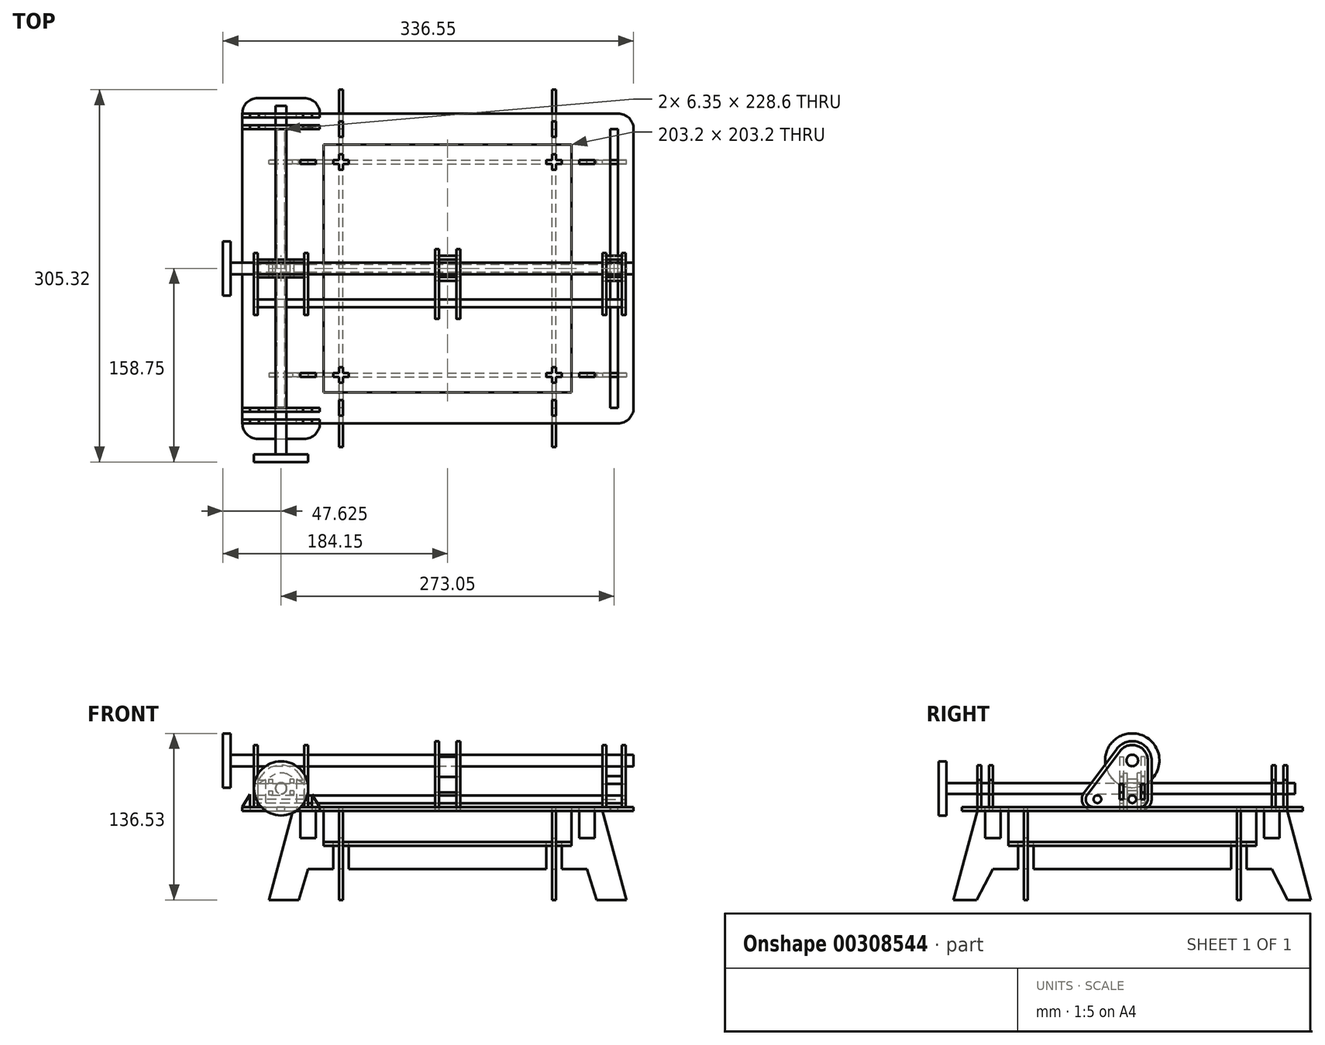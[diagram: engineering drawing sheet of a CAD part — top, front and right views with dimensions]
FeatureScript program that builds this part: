
annotation { "Feature Type Name" : "Feature", "Feature Type Description" : "" }
export const myFeature = defineFeature(function(context is Context, id is Id, definition is map)
    precondition{}
    {
        {
            var Q0;
            Q0=qCreatedBy(makeId("Top.planeOp"),FACE);
            var sketch = newSketch(context, id + "F0", { "sketchPlane" : qUnion([Q0])});
            skLineSegment(sketch, "E0.bottom", {"start": v(-101.6, 101.6) * mm, "end": v(101.6, 101.6) * mm});
            skLineSegment(sketch, "E0.top", {"start": v(-101.6, -101.6) * mm, "end": v(101.6, -101.6) * mm});
            skLineSegment(sketch, "E0.left", {"start": v(-101.6, 101.6) * mm, "end": v(-101.6, -101.6) * mm});
            skLineSegment(sketch, "E0.right", {"start": v(101.6, 101.6) * mm, "end": v(101.6, -101.6) * mm});
            skPoint(sketch, "E0.middle", {"position": v(0, 0) * mm});
            skSolve(sketch);
        }
        {
            var Q0;
            Q0=makeQuery(id+"F0.imprint","IMPRINT",FACE,{"disambiguationData":[TD([[makeQuery(id+"F0.imprint","IMPRINT",EDGE,{"derivedFrom":sQuery(id+"F0.wireOp",EDGE,"E0.bottom")}),-1.0]])]});
            extrude(context, id + "F1", {"entities" : qUnion([Q0]), "oppositeDirection" : true, "depth" : 3.17 * mm});
        }
        {
            var Q0;
            Q0=makeQuery(id+"F1.opExtrude","CAP_FACE",FACE,{"disambiguationData":[OSD([sQuery(id+"F0.wireOp",EDGE,"E0.bottom"),sQuery(id+"F0.wireOp",EDGE,"E0.top"),sQuery(id+"F0.wireOp",EDGE,"E0.left"),sQuery(id+"F0.wireOp",EDGE,"E0.right")])],"isStart":true});
            cPlane(context, id + "F2", {"entities" : qUnion([Q0]), "cplaneType" : CPlaneType.OFFSET, "offset" : 25.4 * mm, "width" : 152.4 * mm, "height" : 152.4 * mm});
        }
        {
            var Q0;
            Q0=qCreatedBy(id+"F2.planeOp",FACE);
            var sketch = newSketch(context, id + "F3", { "sketchPlane" : qUnion([Q0])});
            skLineSegment(sketch, "E1.bottom", {"start": v(-101.6, 101.6) * mm, "end": v(101.6, 101.6) * mm});
            skLineSegment(sketch, "E1.top", {"start": v(-101.6, -101.6) * mm, "end": v(101.6, -101.6) * mm});
            skLineSegment(sketch, "E1.left", {"start": v(-101.6, 101.6) * mm, "end": v(-101.6, -101.6) * mm});
            skLineSegment(sketch, "E1.right", {"start": v(101.6, 101.6) * mm, "end": v(101.6, -101.6) * mm});
            skPoint(sketch, "E1.middle", {"position": v(0, 0) * mm});
            skLineSegment(sketch, "E2.bottom", {"start": v(-114.3, 127) * mm, "end": v(114.3, 127) * mm});
            skLineSegment(sketch, "E2.top", {"start": v(-114.3, -127) * mm, "end": v(114.3, -127) * mm});
            skPoint(sketch, "E3.visualSharp", {"position": v(-127, 127) * mm});
            skPoint(sketch, "E4.visualSharp", {"position": v(127, 127) * mm});
            skPoint(sketch, "E5.visualSharp", {"position": v(127, -127) * mm});
            skPoint(sketch, "E6.visualSharp", {"position": v(-127, -127) * mm});
            skLineSegment(sketch, "E7.right", {"start": v(-152.4, 101.6) * mm, "end": v(-152.4, -101.6) * mm});
            skLineSegment(sketch, "E8.right", {"start": v(152.4, 101.6) * mm, "end": v(152.4, -101.6) * mm});
            skPoint(sketch, "E9.visualSharp", {"position": v(-152.4, 114.3) * mm});
            skPoint(sketch, "E10.visualSharp", {"position": v(-152.4, -114.3) * mm});
            skPoint(sketch, "E11.visualSharp", {"position": v(152.4, -114.3) * mm});
            skPoint(sketch, "E12.visualSharp", {"position": v(152.4, 114.3) * mm});
            skPoint(sketch, "E8.top.start.orphan", {"position": v(127, -114.3) * mm});
            skPoint(sketch, "E7.top.start.orphan", {"position": v(-127, -114.3) * mm});
            skLineSegment(sketch, "E13", {"start": v(-152.4, -101.6) * mm, "end": v(-152.4, -114.3) * mm});
            skLineSegment(sketch, "E14", {"start": v(-114.3, -127) * mm, "end": v(-139.7, -127) * mm});
            skLineSegment(sketch, "E15", {"start": v(114.3, -127) * mm, "end": v(139.7, -127) * mm});
            skLineSegment(sketch, "E16", {"start": v(152.4, -101.6) * mm, "end": v(152.4, -114.3) * mm});
            skLineSegment(sketch, "E17", {"start": v(152.4, 101.6) * mm, "end": v(152.4, 114.3) * mm});
            skLineSegment(sketch, "E18", {"start": v(114.3, 127) * mm, "end": v(139.7, 127) * mm});
            skLineSegment(sketch, "E19", {"start": v(-114.3, 127) * mm, "end": v(-139.7, 127) * mm});
            skLineSegment(sketch, "E20", {"start": v(-152.4, 101.6) * mm, "end": v(-152.4, 114.3) * mm});
            skPoint(sketch, "E21.visualSharp", {"position": v(-152.4, 127) * mm});
            skArc(sketch, "E21.filletArc", {"start": v(-139.7, 127) * mm, "mid": v(-148.68, 123.28) * mm, "end": v(-152.4, 114.3) * mm});
            skPoint(sketch, "E22.visualSharp", {"position": v(152.4, 127) * mm});
            skArc(sketch, "E22.filletArc", {"start": v(152.4, 114.3) * mm, "mid": v(148.68, 123.28) * mm, "end": v(139.7, 127) * mm});
            skPoint(sketch, "E23.visualSharp", {"position": v(152.4, -127) * mm});
            skArc(sketch, "E23.filletArc", {"start": v(139.7, -127) * mm, "mid": v(148.68, -123.28) * mm, "end": v(152.4, -114.3) * mm});
            skPoint(sketch, "E24.visualSharp", {"position": v(-152.4, -127) * mm});
            skArc(sketch, "E24.filletArc", {"start": v(-152.4, -114.3) * mm, "mid": v(-148.68, -123.28) * mm, "end": v(-139.7, -127) * mm});
            skSolve(sketch);
        }
        {
            var Q0;
            Q0=makeQuery(id+"F3.imprint","IMPRINT",FACE,{"disambiguationData":[TD([[makeQuery(id+"F3.imprint","IMPRINT",EDGE,{"derivedFrom":sQuery(id+"F3.wireOp",EDGE,"E1.bottom")}),1.0]])]});
            extrude(context, id + "F4", {"entities" : qUnion([Q0]), "depth" : 3.17 * mm});
        }
        {
            var Q0;
            Q0=makeQuery(id+"F4.opExtrude","CAP_FACE",FACE,{"disambiguationData":[OSD([sQuery(id+"F3.wireOp",EDGE,"E1.bottom"),sQuery(id+"F3.wireOp",EDGE,"E1.top"),sQuery(id+"F3.wireOp",EDGE,"E1.left"),sQuery(id+"F3.wireOp",EDGE,"E1.right"),sQuery(id+"F3.wireOp",EDGE,"E2.bottom"),sQuery(id+"F3.wireOp",EDGE,"E2.top"),sQuery(id+"F3.wireOp",EDGE,"E7.right"),sQuery(id+"F3.wireOp",EDGE,"E8.right"),sQuery(id+"F3.wireOp",EDGE,"E13"),sQuery(id+"F3.wireOp",EDGE,"E14"),sQuery(id+"F3.wireOp",EDGE,"E15"),sQuery(id+"F3.wireOp",EDGE,"E16"),sQuery(id+"F3.wireOp",EDGE,"E17"),sQuery(id+"F3.wireOp",EDGE,"E18"),sQuery(id+"F3.wireOp",EDGE,"E19"),sQuery(id+"F3.wireOp",EDGE,"E20"),sQuery(id+"F3.wireOp",EDGE,"E21.filletArc"),sQuery(id+"F3.wireOp",EDGE,"E22.filletArc"),sQuery(id+"F3.wireOp",EDGE,"E23.filletArc"),sQuery(id+"F3.wireOp",EDGE,"E24.filletArc")])],"isStart":false});
            var sketch = newSketch(context, id + "F5", { "sketchPlane" : qUnion([Q0])});
            skLineSegment(sketch, "E25.bottom", {"start": v(-155.58, -139.7) * mm, "end": v(-117.47, -139.7) * mm});
            skLineSegment(sketch, "E25.top", {"start": v(-155.57, 139.7) * mm, "end": v(-117.48, 139.7) * mm});
            skLineSegment(sketch, "E25.left", {"start": v(-168.28, -127) * mm, "end": v(-168.27, 127) * mm});
            skLineSegment(sketch, "E25.right", {"start": v(-104.77, -127) * mm, "end": v(-104.77, 127) * mm});
            skPoint(sketch, "E25.middle", {"position": v(-136.53, 0) * mm});
            skPoint(sketch, "E26.visualSharp", {"position": v(-104.77, 139.7) * mm});
            skArc(sketch, "E26.filletArc", {"start": v(-104.78, 127) * mm, "mid": v(-108.5, 135.98) * mm, "end": v(-117.48, 139.7) * mm});
            skPoint(sketch, "E27.visualSharp", {"position": v(-168.27, 139.7) * mm});
            skArc(sketch, "E27.filletArc", {"start": v(-155.57, 139.7) * mm, "mid": v(-164.56, 135.98) * mm, "end": v(-168.27, 127) * mm});
            skPoint(sketch, "E28.visualSharp", {"position": v(-168.28, -139.7) * mm});
            skArc(sketch, "E28.filletArc", {"start": v(-168.28, -127) * mm, "mid": v(-164.56, -135.98) * mm, "end": v(-155.58, -139.7) * mm});
            skPoint(sketch, "E29.visualSharp", {"position": v(-104.77, -139.7) * mm});
            skArc(sketch, "E29.filletArc", {"start": v(-117.47, -139.7) * mm, "mid": v(-108.5, -135.98) * mm, "end": v(-104.77, -127) * mm});
            skSolve(sketch);
        }
        {
            var Q0;
            Q0 = qSketchRegion(id + "F5", true);
            extrude(context, id + "F6", {"entities" : qUnion([Q0]), "operationType" : NewBodyOperationType.ADD, "oppositeDirection" : true, "depth" : 3.17 * mm});
        }
        {
            var Q0;
            Q0=makeQuery(id+"F4.opExtrude","CAP_FACE",FACE,{"disambiguationData":[OSD([sQuery(id+"F3.wireOp",EDGE,"E1.bottom"),sQuery(id+"F3.wireOp",EDGE,"E1.top"),sQuery(id+"F3.wireOp",EDGE,"E1.left"),sQuery(id+"F3.wireOp",EDGE,"E1.right"),sQuery(id+"F3.wireOp",EDGE,"E2.bottom"),sQuery(id+"F3.wireOp",EDGE,"E2.top"),sQuery(id+"F3.wireOp",EDGE,"E2.left"),sQuery(id+"F3.wireOp",EDGE,"E2.right"),sQuery(id+"F3.wireOp",EDGE,"E3.filletArc"),sQuery(id+"F3.wireOp",EDGE,"E4.filletArc"),sQuery(id+"F3.wireOp",EDGE,"E5.filletArc"),sQuery(id+"F3.wireOp",EDGE,"E6.filletArc")])],"isStart":false});
            var sketch = newSketch(context, id + "F7", { "sketchPlane" : qUnion([Q0])});
            skLineSegment(sketch, "E30.bottom", {"start": v(-133.35, -114.3) * mm, "end": v(-139.7, -114.3) * mm});
            skLineSegment(sketch, "E30.top", {"start": v(-133.35, 114.3) * mm, "end": v(-139.7, 114.3) * mm});
            skLineSegment(sketch, "E30.left", {"start": v(-133.35, -114.3) * mm, "end": v(-133.35, 114.3) * mm});
            skLineSegment(sketch, "E30.right", {"start": v(-139.7, -114.3) * mm, "end": v(-139.7, 114.3) * mm});
            skPoint(sketch, "E30.middle", {"position": v(-136.53, 0) * mm});
            skLineSegment(sketch, "E31", {"start": v(0, 87.2) * mm, "end": v(0, -86.86) * mm, "construction": true});
            skLineSegment(sketch, "E32.MirrorCS", {"start": v(133.35, -114.3) * mm, "end": v(139.7, -114.3) * mm});
            skLineSegment(sketch, "E33.MirrorCS", {"start": v(133.35, 114.3) * mm, "end": v(139.7, 114.3) * mm});
            skPoint(sketch, "E34.MirrorP", {"position": v(136.53, 0) * mm});
            skLineSegment(sketch, "E35.MirrorCS", {"start": v(133.35, -114.3) * mm, "end": v(133.35, 114.3) * mm});
            skLineSegment(sketch, "E36.MirrorCS", {"start": v(139.7, -114.3) * mm, "end": v(139.7, 114.3) * mm});
            skSolve(sketch);
        }
        {
            var Q0;
            Q0=qCreatedBy(makeId("Right.planeOp"),FACE);
            cPlane(context, id + "F8", {"entities" : qUnion([Q0]), "cplaneType" : CPlaneType.OFFSET, "offset" : 88.9 * mm, "oppositeDirection" : true, "width" : 152.4 * mm, "height" : 152.4 * mm});
        }
        {
            var Q0;
            Q0=qCreatedBy(id+"F8.planeOp",FACE);
            var sketch = newSketch(context, id + "F9", { "sketchPlane" : qUnion([Q0])});
            skLineSegment(sketch, "E37", {"start": v(0, -3.18) * mm, "end": v(80.96, -3.18) * mm});
            skLineSegment(sketch, "E38", {"start": v(101.6, -3.18) * mm, "end": v(101.6, 0) * mm});
            skLineSegment(sketch, "E39", {"start": v(101.6, 0) * mm, "end": v(101.6, 25.4) * mm});
            skLineSegment(sketch, "E40", {"start": v(101.6, 25.4) * mm, "end": v(107.95, 25.4) * mm});
            skLineSegment(sketch, "E41", {"start": v(127, 25.4) * mm, "end": v(146.57, -47.63) * mm});
            skLineSegment(sketch, "E42", {"start": v(146.57, -47.62) * mm, "end": v(127.52, -47.62) * mm});
            skLineSegment(sketch, "E43", {"start": v(127.52, -47.62) * mm, "end": v(114.3, -22.23) * mm});
            skLineSegment(sketch, "E44", {"start": v(114.3, -22.22) * mm, "end": v(88.9, -22.22) * mm});
            skLineSegment(sketch, "E45", {"start": v(0, 51.23) * mm, "end": v(0, 12.05) * mm, "construction": true});
            skLineSegment(sketch, "E46", {"start": v(120.65, 25.4) * mm, "end": v(120.65, 28.58) * mm});
            skLineSegment(sketch, "E47", {"start": v(120.65, 28.58) * mm, "end": v(107.95, 28.58) * mm});
            skLineSegment(sketch, "E48", {"start": v(107.95, 28.58) * mm, "end": v(107.95, 25.4) * mm});
            skLineSegment(sketch, "E49.trimOffspring", {"start": v(120.65, 25.4) * mm, "end": v(127, 25.4) * mm});
            skLineSegment(sketch, "E50", {"start": v(93.66, -3.17) * mm, "end": v(93.66, 0) * mm});
            skLineSegment(sketch, "E51", {"start": v(93.66, 0) * mm, "end": v(80.96, 0) * mm});
            skLineSegment(sketch, "E52", {"start": v(80.96, 0) * mm, "end": v(80.96, -3.17) * mm});
            skLineSegment(sketch, "E53.trimOffspring", {"start": v(93.66, -3.18) * mm, "end": v(101.6, -3.18) * mm});
            skLineSegment(sketch, "E54.MirrorCS", {"start": v(-101.6, -3.18) * mm, "end": v(-101.6, 0) * mm});
            skLineSegment(sketch, "E55.MirrorCS", {"start": v(-101.6, 25.4) * mm, "end": v(-107.95, 25.4) * mm});
            skLineSegment(sketch, "E56.MirrorCS", {"start": v(-80.96, 0) * mm, "end": v(-80.96, -3.18) * mm});
            skLineSegment(sketch, "E57.MirrorCS", {"start": v(-93.66, -3.18) * mm, "end": v(-93.66, 0) * mm});
            skLineSegment(sketch, "E58.MirrorCS", {"start": v(-107.95, 28.58) * mm, "end": v(-107.95, 25.4) * mm});
            skLineSegment(sketch, "E59.MirrorCS", {"start": v(-120.65, 25.4) * mm, "end": v(-127, 25.4) * mm});
            skLineSegment(sketch, "E60.MirrorCS", {"start": v(-120.65, 25.4) * mm, "end": v(-120.65, 28.58) * mm});
            skLineSegment(sketch, "E61.MirrorCS", {"start": v(-93.66, 0) * mm, "end": v(-80.96, 0) * mm});
            skLineSegment(sketch, "E62.MirrorCS", {"start": v(-93.66, -3.18) * mm, "end": v(-101.6, -3.18) * mm});
            skLineSegment(sketch, "E63.MirrorCS", {"start": v(-101.6, 0) * mm, "end": v(-101.6, 25.4) * mm});
            skLineSegment(sketch, "E64.MirrorCS", {"start": v(-127, 25.4) * mm, "end": v(-146.57, -47.63) * mm});
            skLineSegment(sketch, "E65.MirrorCS", {"start": v(-146.57, -47.62) * mm, "end": v(-127.52, -47.62) * mm});
            skLineSegment(sketch, "E66.MirrorCS", {"start": v(-127.52, -47.63) * mm, "end": v(-114.3, -22.23) * mm});
            skLineSegment(sketch, "E67.MirrorCS", {"start": v(-120.65, 28.58) * mm, "end": v(-107.95, 28.58) * mm});
            skLineSegment(sketch, "E68.MirrorCS", {"start": v(0, -3.18) * mm, "end": v(-80.96, -3.18) * mm});
            skLineSegment(sketch, "E69.MirrorCS", {"start": v(-114.3, -22.22) * mm, "end": v(-88.9, -22.22) * mm});
            skLineSegment(sketch, "E70.top", {"start": v(88.9, -10.8) * mm, "end": v(85.73, -10.8) * mm});
            skLineSegment(sketch, "E70.left", {"start": v(88.9, -22.22) * mm, "end": v(88.9, -10.8) * mm});
            skLineSegment(sketch, "E70.right", {"start": v(85.73, -22.22) * mm, "end": v(85.73, -10.8) * mm});
            skLineSegment(sketch, "E71.MirrorCS", {"start": v(-85.73, -22.22) * mm, "end": v(-85.73, -10.8) * mm});
            skLineSegment(sketch, "E72.MirrorCS", {"start": v(-88.9, -22.22) * mm, "end": v(-88.9, -10.8) * mm});
            skLineSegment(sketch, "E73.MirrorCS", {"start": v(-88.9, -10.8) * mm, "end": v(-85.73, -10.8) * mm});
            skLineSegment(sketch, "E74.trimOffspring", {"start": v(-85.73, -22.22) * mm, "end": v(0, -22.23) * mm});
            skLineSegment(sketch, "E75.trimOffspring", {"start": v(85.73, -22.22) * mm, "end": v(0, -22.23) * mm});
            skSolve(sketch);
        }
        {
            var Q0;
            Q0=makeQuery(id+"F9.imprint","IMPRINT",FACE,{"disambiguationData":[TD([[makeQuery(id+"F9.imprint","IMPRINT",EDGE,{"derivedFrom":sQuery(id+"F9.wireOp",EDGE,"E37")}),-1.0]])]});
            extrude(context, id + "F10", {"entities" : qUnion([Q0]), "depth" : 3.17 * mm});
        }
        {
            var Q0;
            Q0=makeQuery(id+"F10.opExtrude","SWEPT_BODY",BODY,{"disambiguationData":[OSD([sQuery(id+"F9.wireOp",EDGE,"E37"),sQuery(id+"F9.wireOp",EDGE,"E38"),sQuery(id+"F9.wireOp",EDGE,"E39"),sQuery(id+"F9.wireOp",EDGE,"E40"),sQuery(id+"F9.wireOp",EDGE,"E41"),sQuery(id+"F9.wireOp",EDGE,"E42"),sQuery(id+"F9.wireOp",EDGE,"E43"),sQuery(id+"F9.wireOp",EDGE,"E44"),sQuery(id+"F9.wireOp",EDGE,"E46"),sQuery(id+"F9.wireOp",EDGE,"E47"),sQuery(id+"F9.wireOp",EDGE,"E48"),sQuery(id+"F9.wireOp",EDGE,"E49.trimOffspring"),sQuery(id+"F9.wireOp",EDGE,"E50"),sQuery(id+"F9.wireOp",EDGE,"E51"),sQuery(id+"F9.wireOp",EDGE,"E52"),sQuery(id+"F9.wireOp",EDGE,"E53.trimOffspring"),sQuery(id+"F9.wireOp",EDGE,"E54.MirrorCS"),sQuery(id+"F9.wireOp",EDGE,"E55.MirrorCS"),sQuery(id+"F9.wireOp",EDGE,"E56.MirrorCS"),sQuery(id+"F9.wireOp",EDGE,"E57.MirrorCS"),sQuery(id+"F9.wireOp",EDGE,"E58.MirrorCS"),sQuery(id+"F9.wireOp",EDGE,"E59.MirrorCS"),sQuery(id+"F9.wireOp",EDGE,"E60.MirrorCS"),sQuery(id+"F9.wireOp",EDGE,"E61.MirrorCS"),sQuery(id+"F9.wireOp",EDGE,"E62.MirrorCS"),sQuery(id+"F9.wireOp",EDGE,"E63.MirrorCS"),sQuery(id+"F9.wireOp",EDGE,"E64.MirrorCS"),sQuery(id+"F9.wireOp",EDGE,"E65.MirrorCS"),sQuery(id+"F9.wireOp",EDGE,"E66.MirrorCS"),sQuery(id+"F9.wireOp",EDGE,"E67.MirrorCS"),sQuery(id+"F9.wireOp",EDGE,"E68.MirrorCS"),sQuery(id+"F9.wireOp",EDGE,"E69.MirrorCS")])]});
            var Q1;
            Q1=qCreatedBy(makeId("Right.planeOp"),FACE);
            mirror(context, id + "F11", {"entities" : qUnion([Q0]), "mirrorPlane" : qUnion([Q1])});
        }
        {
            var Q0;
            Q0=qCreatedBy(makeId("Front.planeOp"),FACE);
            cPlane(context, id + "F12", {"entities" : qUnion([Q0]), "cplaneType" : CPlaneType.OFFSET, "offset" : 88.9 * mm, "width" : 152.4 * mm, "height" : 152.4 * mm});
        }
        {
            var Q0;
            Q0=qCreatedBy(id+"F12.planeOp",FACE);
            var sketch = newSketch(context, id + "F13", { "sketchPlane" : qUnion([Q0])});
            skLineSegment(sketch, "E76", {"start": v(-101.6, -3.18) * mm, "end": v(-101.6, 0) * mm});
            skLineSegment(sketch, "E77", {"start": v(-101.6, 0) * mm, "end": v(-101.6, 25.4) * mm});
            skLineSegment(sketch, "E78", {"start": v(-101.6, 25.4) * mm, "end": v(-107.95, 25.4) * mm});
            skLineSegment(sketch, "E79", {"start": v(-107.95, 25.4) * mm, "end": v(-107.95, 28.58) * mm});
            skLineSegment(sketch, "E80", {"start": v(-107.95, 28.58) * mm, "end": v(-120.65, 28.58) * mm});
            skLineSegment(sketch, "E81", {"start": v(-120.65, 28.58) * mm, "end": v(-120.65, 25.4) * mm});
            skLineSegment(sketch, "E82", {"start": v(-120.65, 25.4) * mm, "end": v(-127, 25.4) * mm});
            skLineSegment(sketch, "E83", {"start": v(-127, 25.4) * mm, "end": v(-146.57, -47.63) * mm});
            skLineSegment(sketch, "E84", {"start": v(-146.57, -47.63) * mm, "end": v(-122.04, -47.63) * mm});
            skLineSegment(sketch, "E85", {"start": v(-122.04, -47.63) * mm, "end": v(-114.3, -22.22) * mm});
            skLineSegment(sketch, "E86", {"start": v(-114.3, -22.22) * mm, "end": v(0, -22.22) * mm});
            skLineSegment(sketch, "E87.0", {"start": v(0, -3.18) * mm, "end": v(-80.96, -3.18) * mm});
            skPoint(sketch, "E88.start.orphan", {"position": v(0, -11.05) * mm});
            skLineSegment(sketch, "E89", {"start": v(-93.66, -3.18) * mm, "end": v(-93.66, 0) * mm});
            skLineSegment(sketch, "E90", {"start": v(-93.66, 0) * mm, "end": v(-88.9, 0) * mm});
            skLineSegment(sketch, "E91", {"start": v(-80.96, 0) * mm, "end": v(-80.96, -3.18) * mm});
            skLineSegment(sketch, "E92", {"start": v(0, 50.7) * mm, "end": v(0, 10.1) * mm, "construction": true});
            skLineSegment(sketch, "E93.MirrorCS", {"start": v(101.6, -3.18) * mm, "end": v(101.6, 0) * mm});
            skLineSegment(sketch, "E94.MirrorCS", {"start": v(107.95, 25.4) * mm, "end": v(107.95, 28.58) * mm});
            skLineSegment(sketch, "E95.MirrorCS", {"start": v(120.65, 28.58) * mm, "end": v(120.65, 25.4) * mm});
            skLineSegment(sketch, "E96.MirrorCS", {"start": v(120.65, 25.4) * mm, "end": v(127, 25.4) * mm});
            skLineSegment(sketch, "E97.MirrorCS", {"start": v(101.6, 25.4) * mm, "end": v(107.95, 25.4) * mm});
            skLineSegment(sketch, "E98.MirrorCS", {"start": v(107.95, 28.58) * mm, "end": v(120.65, 28.58) * mm});
            skLineSegment(sketch, "E99.MirrorCS", {"start": v(122.04, -47.63) * mm, "end": v(114.3, -22.22) * mm});
            skLineSegment(sketch, "E100.MirrorCS", {"start": v(80.96, 0) * mm, "end": v(80.96, -3.17) * mm});
            skLineSegment(sketch, "E101.MirrorCS", {"start": v(93.66, 0) * mm, "end": v(88.9, 0) * mm});
            skLineSegment(sketch, "E102.MirrorCS", {"start": v(93.66, -3.17) * mm, "end": v(93.66, 0) * mm});
            skLineSegment(sketch, "E103.MirrorCS", {"start": v(101.6, 0) * mm, "end": v(101.6, 25.4) * mm});
            skLineSegment(sketch, "E104.MirrorCS", {"start": v(146.57, -47.63) * mm, "end": v(122.04, -47.63) * mm});
            skLineSegment(sketch, "E105.MirrorCS", {"start": v(127, 25.4) * mm, "end": v(146.57, -47.63) * mm});
            skLineSegment(sketch, "E106.MirrorCS", {"start": v(114.3, -22.22) * mm, "end": v(0, -22.22) * mm});
            skLineSegment(sketch, "E107.MirrorCS", {"start": v(0, -3.18) * mm, "end": v(80.96, -3.18) * mm});
            skLineSegment(sketch, "E108.trimOffspring", {"start": v(-93.66, -3.18) * mm, "end": v(-101.6, -3.18) * mm});
            skLineSegment(sketch, "E109.trimOffspring", {"start": v(93.66, -3.18) * mm, "end": v(101.6, -3.18) * mm});
            skLineSegment(sketch, "E110.top", {"start": v(-88.9, -11.43) * mm, "end": v(-85.73, -11.43) * mm});
            skLineSegment(sketch, "E110.left", {"start": v(-88.9, 0) * mm, "end": v(-88.9, -11.43) * mm});
            skLineSegment(sketch, "E110.right", {"start": v(-85.73, 0) * mm, "end": v(-85.73, -11.43) * mm});
            skLineSegment(sketch, "E111.MirrorCS", {"start": v(85.73, 0) * mm, "end": v(85.73, -11.43) * mm});
            skLineSegment(sketch, "E112.MirrorCS", {"start": v(88.9, 0) * mm, "end": v(88.9, -11.43) * mm});
            skLineSegment(sketch, "E113.MirrorCS", {"start": v(88.9, -11.43) * mm, "end": v(85.73, -11.43) * mm});
            skLineSegment(sketch, "E114.trimOffspring", {"start": v(-85.73, 0) * mm, "end": v(-80.96, 0) * mm});
            skLineSegment(sketch, "E115.trimOffspring", {"start": v(85.73, 0) * mm, "end": v(80.96, 0) * mm});
            skSolve(sketch);
        }
        {
            var Q0;
            {var subQ2=sQuery(id+"F13.wireOp",EDGE,"E76");Q0=makeQuery(id+"F13.imprint","IMPRINT",FACE,{"disambiguationData":[TD([[makeQuery(id+"F13.imprint","IMPRINT",EDGE,{"derivedFrom":subQ2}),1.0]])]});}
            extrude(context, id + "F14", {"entities" : qUnion([Q0]), "oppositeDirection" : true, "depth" : 3.17 * mm});
        }
        {
            var Q0;
            Q0=makeQuery(id+"F14.opExtrude","SWEPT_BODY",BODY,{"disambiguationData":[OSD([sQuery(id+"F13.wireOp",EDGE,"E76"),sQuery(id+"F13.wireOp",EDGE,"E77"),sQuery(id+"F13.wireOp",EDGE,"E78"),sQuery(id+"F13.wireOp",EDGE,"E79"),sQuery(id+"F13.wireOp",EDGE,"E80"),sQuery(id+"F13.wireOp",EDGE,"E81"),sQuery(id+"F13.wireOp",EDGE,"E82"),sQuery(id+"F13.wireOp",EDGE,"E83"),sQuery(id+"F13.wireOp",EDGE,"E84"),sQuery(id+"F13.wireOp",EDGE,"E85"),sQuery(id+"F13.wireOp",EDGE,"E86"),sQuery(id+"F13.wireOp",EDGE,"E87.0"),sQuery(id+"F13.wireOp",EDGE,"E89"),sQuery(id+"F13.wireOp",EDGE,"E90"),sQuery(id+"F13.wireOp",EDGE,"E91"),sQuery(id+"F13.wireOp",EDGE,"E98.MirrorCS"),sQuery(id+"F13.wireOp",EDGE,"E95.MirrorCS"),sQuery(id+"F13.wireOp",EDGE,"E96.MirrorCS"),sQuery(id+"F13.wireOp",EDGE,"E93.MirrorCS"),sQuery(id+"F13.wireOp",EDGE,"E94.MirrorCS"),sQuery(id+"F13.wireOp",EDGE,"E97.MirrorCS"),sQuery(id+"F13.wireOp",EDGE,"E102.MirrorCS"),sQuery(id+"F13.wireOp",EDGE,"E101.MirrorCS"),sQuery(id+"F13.wireOp",EDGE,"E100.MirrorCS"),sQuery(id+"F13.wireOp",EDGE,"E104.MirrorCS"),sQuery(id+"F13.wireOp",EDGE,"E105.MirrorCS"),sQuery(id+"F13.wireOp",EDGE,"E103.MirrorCS"),sQuery(id+"F13.wireOp",EDGE,"E99.MirrorCS"),sQuery(id+"F13.wireOp",EDGE,"E106.MirrorCS"),sQuery(id+"F13.wireOp",EDGE,"E107.MirrorCS"),sQuery(id+"F13.wireOp",EDGE,"E108.trimOffspring"),sQuery(id+"F13.wireOp",EDGE,"E109.trimOffspring")])]});
            var Q1;
            Q1=qCreatedBy(makeId("Front.planeOp"),FACE);
            mirror(context, id + "F15", {"entities" : qUnion([Q0]), "mirrorPlane" : qUnion([Q1])});
        }
        {
            var Q0;
            Q0=makeQuery(id+"F7.imprint","IMPRINT",FACE,{"disambiguationData":[TD([[makeQuery(id+"F7.imprint","IMPRINT",EDGE,{"derivedFrom":sQuery(id+"F7.wireOp",EDGE,"E30.bottom")}),-1.0]])]});
            var Q1;
            Q1=makeQuery(id+"F7.imprint","IMPRINT",FACE,{"disambiguationData":[TD([[makeQuery(id+"F7.imprint","IMPRINT",EDGE,{"derivedFrom":sQuery(id+"F7.wireOp",EDGE,"E32.MirrorCS")}),1.0]])]});
            extrude(context, id + "F16", {"entities" : qUnion([Q0, Q1]), "operationType" : NewBodyOperationType.REMOVE, "oppositeDirection" : true, "depth" : 8.13 * mm});
        }
        {
            var Q0;
            Q0=qCreatedBy(makeId("Front.planeOp"),FACE);
            cPlane(context, id + "F17", {"entities" : qUnion([Q0]), "cplaneType" : CPlaneType.OFFSET, "offset" : 114.3 * mm, "width" : 152.4 * mm, "height" : 152.4 * mm});
        }
        {
            var Q0;
            Q0=qCreatedBy(id+"F17.planeOp",FACE);
            var sketch = newSketch(context, id + "F18", { "sketchPlane" : qUnion([Q0])});
            skCircle(sketch, "E116", {"center": v(-136.53, 43.82) * mm, "radius": 4.76 * mm});
            skArc(sketch, "E117", {"start": v(-120.3, 53.8) * mm, "mid": v(-136.53, 62.87) * mm, "end": v(-152.75, 53.8) * mm});
            skLineSegment(sketch, "E118", {"start": v(-168.28, 28.58) * mm, "end": v(-161.93, 28.58) * mm});
            skLineSegment(sketch, "E119", {"start": v(-161.93, 28.58) * mm, "end": v(-161.93, 25.4) * mm});
            skLineSegment(sketch, "E120", {"start": v(-161.93, 25.4) * mm, "end": v(-149.23, 25.4) * mm});
            skLineSegment(sketch, "E121", {"start": v(-149.23, 25.4) * mm, "end": v(-149.23, 28.58) * mm});
            skLineSegment(sketch, "E122", {"start": v(-123.83, 28.58) * mm, "end": v(-123.83, 25.4) * mm});
            skLineSegment(sketch, "E123", {"start": v(-123.83, 25.4) * mm, "end": v(-111.13, 25.4) * mm});
            skLineSegment(sketch, "E124", {"start": v(-111.12, 25.4) * mm, "end": v(-111.12, 28.58) * mm});
            skLineSegment(sketch, "E125.trimOffspring", {"start": v(-111.12, 28.58) * mm, "end": v(-104.78, 28.58) * mm});
            skLineSegment(sketch, "E126.trimOffspring", {"start": v(-149.23, 28.58) * mm, "end": v(-123.83, 28.58) * mm});
            skLineSegment(sketch, "E127", {"start": v(-168.28, 28.58) * mm, "end": v(-152.75, 53.8) * mm});
            skLineSegment(sketch, "E128", {"start": v(-104.78, 28.58) * mm, "end": v(-120.3, 53.8) * mm});
            skSolve(sketch);
        }
        {
            var Q0;
            Q0=makeQuery(id+"F18.imprint","IMPRINT",FACE,{"disambiguationData":[TD([[makeQuery(id+"F18.imprint","IMPRINT",EDGE,{"derivedFrom":sQuery(id+"F18.wireOp",EDGE,"E116")}),-1.0]])]});
            extrude(context, id + "F19", {"entities" : qUnion([Q0]), "depth" : 3.17 * mm});
        }
        {
            var Q0;
            Q0=qCreatedBy(id+"F17.planeOp",FACE);
            cPlane(context, id + "F20", {"entities" : qUnion([Q0]), "cplaneType" : CPlaneType.OFFSET, "offset" : 6.35 * mm, "width" : 152.4 * mm, "height" : 152.4 * mm});
        }
        {
            var Q0;
            Q0=makeQuery(id+"F19.opExtrude","SWEPT_BODY",BODY,{"disambiguationData":[OSD([sQuery(id+"F18.wireOp",EDGE,"E116"),sQuery(id+"F18.wireOp",EDGE,"E117"),sQuery(id+"F18.wireOp",EDGE,"38bzoTGT-MK2d-pk2N-3JFI-UJTJc2NmZi06"),sQuery(id+"F18.wireOp",EDGE,"pucSDfX4-3BOz-H23i-j3uv-TdQ4Dl5jIXsU"),sQuery(id+"F18.wireOp",EDGE,"E118")])]});
            var Q1;
            Q1=qCreatedBy(id+"F20.planeOp",FACE);
            mirror(context, id + "F21", {"entities" : qUnion([Q0]), "mirrorPlane" : qUnion([Q1])});
        }
        {
            var Q0;
            Q0=makeQuery(id+"F21.opPattern","COPY",BODY,{"derivedFrom":makeQuery(id+"F19.opExtrude","SWEPT_BODY",BODY,{"disambiguationData":[OSD([sQuery(id+"F18.wireOp",EDGE,"E116"),sQuery(id+"F18.wireOp",EDGE,"E117"),sQuery(id+"F18.wireOp",EDGE,"38bzoTGT-MK2d-pk2N-3JFI-UJTJc2NmZi06"),sQuery(id+"F18.wireOp",EDGE,"pucSDfX4-3BOz-H23i-j3uv-TdQ4Dl5jIXsU"),sQuery(id+"F18.wireOp",EDGE,"E118")])]}),"instanceName":"1"});
            var Q1;
            Q1=makeQuery(id+"F19.opExtrude","SWEPT_BODY",BODY,{"disambiguationData":[OSD([sQuery(id+"F18.wireOp",EDGE,"E116"),sQuery(id+"F18.wireOp",EDGE,"E117"),sQuery(id+"F18.wireOp",EDGE,"38bzoTGT-MK2d-pk2N-3JFI-UJTJc2NmZi06"),sQuery(id+"F18.wireOp",EDGE,"pucSDfX4-3BOz-H23i-j3uv-TdQ4Dl5jIXsU"),sQuery(id+"F18.wireOp",EDGE,"E118")])]});
            var Q2;
            Q2=qCreatedBy(makeId("Front.planeOp"),FACE);
            mirror(context, id + "F22", {"entities" : qUnion([Q0, Q1]), "mirrorPlane" : qUnion([Q2])});
        }
        {
            var Q0;
            Q0=qCreatedBy(makeId("Right.planeOp"),FACE);
            cPlane(context, id + "F23", {"entities" : qUnion([Q0]), "cplaneType" : CPlaneType.OFFSET, "offset" : 114.3 * mm, "oppositeDirection" : true, "width" : 152.4 * mm, "height" : 152.4 * mm});
        }
        {
            var Q0;
            Q0=qCreatedBy(makeId("Right.planeOp"),FACE);
            cPlane(context, id + "F24", {"entities" : qUnion([Q0]), "cplaneType" : CPlaneType.OFFSET, "offset" : 136.53 * mm, "oppositeDirection" : true, "width" : 152.4 * mm, "height" : 152.4 * mm});
        }
        {
            var Q0;
            Q0=qCreatedBy(id+"F23.planeOp",FACE);
            var sketch = newSketch(context, id + "F25", { "sketchPlane" : qUnion([Q0])});
            skCircle(sketch, "E129", {"center": v(0, 66.68) * mm, "radius": 4.76 * mm});
            skArc(sketch, "E130", {"start": v(12.7, 66.68) * mm, "mid": v(4.02, 78.72) * mm, "end": v(-10.16, 74.3) * mm});
            skLineSegment(sketch, "E131", {"start": v(12.7, 66.68) * mm, "end": v(12.7, 34.93) * mm});
            skLineSegment(sketch, "E132", {"start": v(-10.16, 74.3) * mm, "end": v(-36.83, 38.73) * mm});
            skLineSegment(sketch, "E133", {"start": v(6.35, 28.58) * mm, "end": v(-31.75, 28.58) * mm});
            skCircle(sketch, "E134", {"center": v(0, 34.93) * mm, "radius": 3.18 * mm});
            skCircle(sketch, "E135", {"center": v(-28.57, 34.92) * mm, "radius": 3.18 * mm});
            skPoint(sketch, "E136.visualSharp", {"position": v(12.7, 28.58) * mm});
            skPoint(sketch, "E137.visualSharp", {"position": v(-44.45, 28.57) * mm});
            skArc(sketch, "E138.filletArc", {"start": v(6.35, 28.58) * mm, "mid": v(10.84, 30.43) * mm, "end": v(12.7, 34.93) * mm});
            skArc(sketch, "E139.filletArc", {"start": v(-36.83, 38.73) * mm, "mid": v(-37.43, 32.09) * mm, "end": v(-31.75, 28.57) * mm});
            skSolve(sketch);
        }
        {
            var Q0;
            Q0=makeQuery(id+"F25.imprint","IMPRINT",FACE,{"disambiguationData":[TD([[makeQuery(id+"F25.imprint","IMPRINT",EDGE,{"derivedFrom":sQuery(id+"F25.wireOp",EDGE,"E129")}),-1.0]])]});
            extrude(context, id + "F26", {"entities" : qUnion([Q0]), "oppositeDirection" : true, "depth" : 3.17 * mm});
        }
        {
            var Q0;
            Q0=makeQuery(id+"F26.opExtrude","SWEPT_BODY",BODY,{"disambiguationData":[OSD([sQuery(id+"F25.wireOp",EDGE,"E129"),sQuery(id+"F25.wireOp",EDGE,"E130"),sQuery(id+"F25.wireOp",EDGE,"E131"),sQuery(id+"F25.wireOp",EDGE,"E132"),sQuery(id+"F25.wireOp",EDGE,"E133")])]});
            var Q1;
            Q1=qCreatedBy(id+"F24.planeOp",FACE);
            mirror(context, id + "F27", {"entities" : qUnion([Q0]), "mirrorPlane" : qUnion([Q1])});
        }
        {
            var Q0;
            Q0=qCreatedBy(makeId("Front.planeOp"),FACE);
            cPlane(context, id + "F28", {"entities" : qUnion([Q0]), "cplaneType" : CPlaneType.OFFSET, "offset" : 7.14 * mm, "width" : 152.4 * mm, "height" : 152.4 * mm});
        }
        {
            var Q0;
            Q0=qCreatedBy(makeId("Front.planeOp"),FACE);
            cPlane(context, id + "F29", {"entities" : qUnion([Q0]), "cplaneType" : CPlaneType.OFFSET, "offset" : 4.17 * mm, "width" : 152.4 * mm, "height" : 152.4 * mm});
        }
        {
            var Q0;
            Q0=qCreatedBy(id+"F29.planeOp",FACE);
            var sketch = newSketch(context, id + "F30", { "sketchPlane" : qUnion([Q0])});
            skLineSegment(sketch, "E140.bottom", {"start": v(-155.58, 28.58) * mm, "end": v(-139.7, 28.58) * mm});
            skLineSegment(sketch, "E140.top", {"start": v(-155.58, 60.33) * mm, "end": v(-117.48, 60.33) * mm});
            skLineSegment(sketch, "E140.left", {"start": v(-155.58, 28.58) * mm, "end": v(-155.58, 34.93) * mm});
            skLineSegment(sketch, "E140.right", {"start": v(-117.48, 28.58) * mm, "end": v(-117.48, 34.93) * mm});
            skCircle(sketch, "E141", {"center": v(-136.53, 43.82) * mm, "radius": 4.76 * mm});
            skLineSegment(sketch, "E142", {"start": v(-155.58, 47.63) * mm, "end": v(-158.75, 47.63) * mm});
            skLineSegment(sketch, "E143", {"start": v(-158.75, 47.63) * mm, "end": v(-158.75, 34.93) * mm});
            skLineSegment(sketch, "E144", {"start": v(-158.75, 34.93) * mm, "end": v(-155.58, 34.93) * mm});
            skLineSegment(sketch, "E145", {"start": v(-117.48, 47.63) * mm, "end": v(-114.3, 47.63) * mm});
            skLineSegment(sketch, "E146", {"start": v(-114.3, 47.63) * mm, "end": v(-114.3, 34.93) * mm});
            skLineSegment(sketch, "E147", {"start": v(-114.3, 34.93) * mm, "end": v(-117.48, 34.93) * mm});
            skLineSegment(sketch, "E148.trimOffspring", {"start": v(-117.48, 47.63) * mm, "end": v(-117.48, 60.33) * mm});
            skLineSegment(sketch, "E149.trimOffspring", {"start": v(-155.58, 47.63) * mm, "end": v(-155.58, 60.33) * mm});
            skLineSegment(sketch, "E150", {"start": v(-139.7, 28.58) * mm, "end": v(-139.7, 25.4) * mm});
            skLineSegment(sketch, "E151", {"start": v(-139.7, 25.4) * mm, "end": v(-133.35, 25.4) * mm});
            skLineSegment(sketch, "E152", {"start": v(-133.35, 25.4) * mm, "end": v(-133.35, 28.58) * mm});
            skLineSegment(sketch, "E153.trimOffspring", {"start": v(-133.35, 28.58) * mm, "end": v(-117.48, 28.58) * mm});
            skArc(sketch, "E154", {"start": v(-130.27, 54.87) * mm, "mid": v(-136.53, 56.52) * mm, "end": v(-142.78, 54.87) * mm});
            skLineSegment(sketch, "E155", {"start": v(-155.58, 47.63) * mm, "end": v(-142.78, 54.87) * mm});
            skLineSegment(sketch, "E156", {"start": v(-117.48, 47.63) * mm, "end": v(-130.27, 54.87) * mm});
            skSolve(sketch);
        }
        {
            var Q0;
            Q0=makeQuery(id+"F30.imprint","IMPRINT",FACE,{"disambiguationData":[TD([[makeQuery(id+"F30.imprint","IMPRINT",EDGE,{"derivedFrom":sQuery(id+"F30.wireOp",EDGE,"E140.bottom")}),1.0]])]});
            extrude(context, id + "F31", {"entities" : qUnion([Q0]), "depth" : 3.17 * mm});
        }
        {
            var Q0;
            Q0=makeQuery(id+"F31.opExtrude","SWEPT_BODY",BODY,{"disambiguationData":[OSD([sQuery(id+"F30.wireOp",EDGE,"E140.bottom"),sQuery(id+"F30.wireOp",EDGE,"E140.top"),sQuery(id+"F30.wireOp",EDGE,"E140.left"),sQuery(id+"F30.wireOp",EDGE,"E140.right"),sQuery(id+"F30.wireOp",EDGE,"E141"),sQuery(id+"F30.wireOp",EDGE,"E142"),sQuery(id+"F30.wireOp",EDGE,"E143"),sQuery(id+"F30.wireOp",EDGE,"E144"),sQuery(id+"F30.wireOp",EDGE,"E145"),sQuery(id+"F30.wireOp",EDGE,"E146"),sQuery(id+"F30.wireOp",EDGE,"E147"),sQuery(id+"F30.wireOp",EDGE,"E148.trimOffspring"),sQuery(id+"F30.wireOp",EDGE,"E149.trimOffspring"),sQuery(id+"F30.wireOp",EDGE,"E150"),sQuery(id+"F30.wireOp",EDGE,"E151"),sQuery(id+"F30.wireOp",EDGE,"E152"),sQuery(id+"F30.wireOp",EDGE,"E153.trimOffspring")])]});
            var Q1;
            Q1=qCreatedBy(makeId("Front.planeOp"),FACE);
            mirror(context, id + "F32", {"entities" : qUnion([Q0]), "mirrorPlane" : qUnion([Q1])});
        }
        {
            var Q0;
            Q0=qCreatedBy(makeId("Right.planeOp"),FACE);
            cPlane(context, id + "F33", {"entities" : qUnion([Q0]), "cplaneType" : CPlaneType.OFFSET, "offset" : 127 * mm, "width" : 152.4 * mm, "height" : 152.4 * mm});
        }
        {
            var Q0;
            Q0=qCreatedBy(id+"F33.planeOp",FACE);
            var sketch = newSketch(context, id + "F34", { "sketchPlane" : qUnion([Q0])});
            skArc(sketch, "E157.0", {"start": v(12.7, 66.68) * mm, "mid": v(4.02, 78.72) * mm, "end": v(-10.16, 74.3) * mm});
            skLineSegment(sketch, "E158.0", {"start": v(12.7, 66.68) * mm, "end": v(12.7, 66.68) * mm});
            skLineSegment(sketch, "E159.0", {"start": v(-10.16, 74.3) * mm, "end": v(-10.16, 74.3) * mm});
            skCircle(sketch, "E160.0", {"center": v(0, 66.68) * mm, "radius": 4.76 * mm});
            skCircle(sketch, "E161.0", {"center": v(-28.57, 34.92) * mm, "radius": 3.18 * mm});
            skCircle(sketch, "E162.0", {"center": v(0, 34.93) * mm, "radius": 3.18 * mm});
            skLineSegment(sketch, "E163.0", {"start": v(-10.16, 74.3) * mm, "end": v(-36.83, 38.73) * mm});
            skArc(sketch, "E164.0", {"start": v(-36.83, 38.73) * mm, "mid": v(-37.43, 32.09) * mm, "end": v(-31.75, 28.57) * mm});
            skArc(sketch, "E165.0", {"start": v(6.35, 28.58) * mm, "mid": v(10.84, 30.43) * mm, "end": v(12.7, 34.93) * mm});
            skLineSegment(sketch, "E166.0", {"start": v(6.35, 28.58) * mm, "end": v(-31.75, 28.58) * mm});
            skLineSegment(sketch, "E167.0", {"start": v(12.7, 66.68) * mm, "end": v(12.7, 34.93) * mm});
            skSolve(sketch);
        }
        {
            var Q0;
            Q0=makeQuery(id+"F34.imprint","IMPRINT",FACE,{"disambiguationData":[TD([[makeQuery(id+"F34.imprint","IMPRINT",EDGE,{"derivedFrom":sQuery(id+"F34.wireOp",EDGE,"E160.0")}),-1.0]])]});
            extrude(context, id + "F35", {"entities" : qUnion([Q0]), "depth" : 3.17 * mm});
        }
        {
            var Q0;
            Q0=qCreatedBy(makeId("Right.planeOp"),FACE);
            cPlane(context, id + "F36", {"entities" : qUnion([Q0]), "cplaneType" : CPlaneType.OFFSET, "offset" : 136.53 * mm, "width" : 152.4 * mm, "height" : 152.4 * mm});
        }
        {
            var Q0;
            Q0=makeQuery(id+"F35.opExtrude","SWEPT_BODY",BODY,{"disambiguationData":[OSD([sQuery(id+"F34.wireOp",EDGE,"E157.0"),sQuery(id+"F34.wireOp",EDGE,"E158.0"),sQuery(id+"F34.wireOp",EDGE,"628ac780-78d9-4351-907e-1ec801662de6.0"),sQuery(id+"F34.wireOp",EDGE,"E159.0"),sQuery(id+"F34.wireOp",EDGE,"E160.0")])]});
            var Q1;
            Q1=qCreatedBy(id+"F36.planeOp",FACE);
            mirror(context, id + "F37", {"entities" : qUnion([Q0]), "mirrorPlane" : qUnion([Q1])});
        }
        {
            var Q0;
            Q0=qCreatedBy(makeId("Right.planeOp"),FACE);
            var sketch = newSketch(context, id + "F38", { "sketchPlane" : qUnion([Q0])});
            skCircle(sketch, "E168.0", {"center": v(-28.57, 34.92) * mm, "radius": 3.18 * mm});
            skCircle(sketch, "E169.0", {"center": v(0, 34.93) * mm, "radius": 3.18 * mm});
            skSolve(sketch);
        }
        {
            var Q0;
            Q0 = qSketchRegion(id + "F38", true);
            extrude(context, id + "F39", {"entities" : qUnion([Q0]), "depth" : 146.05 * mm, "hasSecondDirection" : true, "secondDirectionOppositeDirection" : true, "secondDirectionDepth" : 158.75 * mm});
        }
        {
            var Q0;
            Q0=qCreatedBy(makeId("Right.planeOp"),FACE);
            cPlane(context, id + "F40", {"entities" : qUnion([Q0]), "cplaneType" : CPlaneType.OFFSET, "offset" : 7.14 * mm, "width" : 152.4 * mm, "height" : 152.4 * mm});
        }
        {
            var Q0;
            Q0=qCreatedBy(id+"F40.planeOp",FACE);
            var sketch = newSketch(context, id + "F41", { "sketchPlane" : qUnion([Q0])});
            skCircle(sketch, "E170", {"center": v(0, 66.68) * mm, "radius": 4.76 * mm});
            skArc(sketch, "E171", {"start": v(15.88, 66.68) * mm, "mid": v(5.02, 81.74) * mm, "end": v(-12.7, 76.2) * mm});
            skLineSegment(sketch, "E172", {"start": v(-12.7, 76.2) * mm, "end": v(-39.37, 40.64) * mm});
            skLineSegment(sketch, "E173", {"start": v(15.88, 66.68) * mm, "end": v(15.88, 34.93) * mm});
            skLineSegment(sketch, "E174", {"start": v(-31.75, 25.4) * mm, "end": v(6.35, 25.4) * mm});
            skPoint(sketch, "E175.visualSharp", {"position": v(-50.8, 25.4) * mm});
            skArc(sketch, "E175.filletArc", {"start": v(-39.37, 40.64) * mm, "mid": v(-40.27, 30.67) * mm, "end": v(-31.75, 25.4) * mm});
            skPoint(sketch, "E176.visualSharp", {"position": v(15.88, 25.4) * mm});
            skArc(sketch, "E176.filletArc", {"start": v(6.35, 25.4) * mm, "mid": v(13.09, 28.19) * mm, "end": v(15.88, 34.93) * mm});
            skCircle(sketch, "E177", {"center": v(0, 34.93) * mm, "radius": 3.3 * mm});
            skCircle(sketch, "E178", {"center": v(-28.57, 34.92) * mm, "radius": 3.3 * mm});
            skSolve(sketch);
        }
        {
            var Q0;
            Q0=makeQuery(id+"F41.imprint","IMPRINT",FACE,{"disambiguationData":[TD([[makeQuery(id+"F41.imprint","IMPRINT",EDGE,{"derivedFrom":sQuery(id+"F41.wireOp",EDGE,"E170")}),-1.0]])]});
            extrude(context, id + "F42", {"entities" : qUnion([Q0]), "depth" : 3.17 * mm});
        }
        {
            var Q0;
            Q0=makeQuery(id+"F42.opExtrude","SWEPT_BODY",BODY,{"disambiguationData":[OSD([sQuery(id+"F41.wireOp",EDGE,"E170"),sQuery(id+"F41.wireOp",EDGE,"E171"),sQuery(id+"F41.wireOp",EDGE,"E172"),sQuery(id+"F41.wireOp",EDGE,"E173"),sQuery(id+"F41.wireOp",EDGE,"E174"),sQuery(id+"F41.wireOp",EDGE,"E175.filletArc"),sQuery(id+"F41.wireOp",EDGE,"E176.filletArc"),sQuery(id+"F41.wireOp",EDGE,"E177"),sQuery(id+"F41.wireOp",EDGE,"E178")])]});
            var Q1;
            Q1=qCreatedBy(makeId("Right.planeOp"),FACE);
            mirror(context, id + "F43", {"entities" : qUnion([Q0]), "mirrorPlane" : qUnion([Q1])});
        }
        {
            var Q0;
            Q0=qCreatedBy(makeId("Right.planeOp"),FACE);
            var sketch = newSketch(context, id + "F44", { "sketchPlane" : qUnion([Q0])});
            skCircle(sketch, "E179", {"center": v(0, 66.68) * mm, "radius": 4.76 * mm});
            skSolve(sketch);
        }
        {
            var Q0;
            Q0=makeQuery(id+"F44.imprint","IMPRINT",FACE,{"disambiguationData":[TD([[makeQuery(id+"F44.imprint","IMPRINT",EDGE,{"derivedFrom":sQuery(id+"F44.wireOp",EDGE,"E179")}),1.0]])]});
            extrude(context, id + "F45", {"entities" : qUnion([Q0]), "depth" : 152.4 * mm, "hasSecondDirection" : true, "secondDirectionOppositeDirection" : true, "secondDirectionDepth" : 177.8 * mm});
        }
        {
            var Q0;
            Q0=qCreatedBy(makeId("Front.planeOp"),FACE);
            var sketch = newSketch(context, id + "F46", { "sketchPlane" : qUnion([Q0])});
            skCircle(sketch, "E180", {"center": v(-136.53, 43.82) * mm, "radius": 4.45 * mm});
            skSolve(sketch);
        }
        {
            var Q0;
            Q0=makeQuery(id+"F46.imprint","IMPRINT",FACE,{"disambiguationData":[TD([[makeQuery(id+"F46.imprint","IMPRINT",EDGE,{"derivedFrom":sQuery(id+"F46.wireOp",EDGE,"E180")}),1.0]])]});
            extrude(context, id + "F47", {"entities" : qUnion([Q0]), "depth" : 152.4 * mm, "hasSecondDirection" : true, "secondDirectionOppositeDirection" : true, "secondDirectionDepth" : 133.35 * mm});
        }
        {
            var Q0;
            Q0=qCreatedBy(id+"F28.planeOp",FACE);
            var sketch = newSketch(context, id + "F48", { "sketchPlane" : qUnion([Q0])});
            skLineSegment(sketch, "E181.bottom", {"start": v(130.18, 53.98) * mm, "end": v(142.88, 53.98) * mm});
            skLineSegment(sketch, "E181.top", {"start": v(130.18, 28.58) * mm, "end": v(133.48, 28.58) * mm});
            skLineSegment(sketch, "E181.left", {"start": v(130.18, 53.98) * mm, "end": v(130.18, 47.62) * mm});
            skLineSegment(sketch, "E181.right", {"start": v(142.88, 53.98) * mm, "end": v(142.88, 47.63) * mm});
            skLineSegment(sketch, "E182", {"start": v(133.48, 28.58) * mm, "end": v(133.48, 25.4) * mm});
            skLineSegment(sketch, "E183", {"start": v(133.48, 25.4) * mm, "end": v(139.57, 25.4) * mm});
            skLineSegment(sketch, "E184", {"start": v(139.57, 25.4) * mm, "end": v(139.57, 28.58) * mm});
            skLineSegment(sketch, "E185", {"start": v(130.18, 47.62) * mm, "end": v(127, 47.62) * mm});
            skLineSegment(sketch, "E186", {"start": v(127, 47.63) * mm, "end": v(127, 34.93) * mm});
            skLineSegment(sketch, "E187", {"start": v(127, 34.92) * mm, "end": v(130.18, 34.92) * mm});
            skLineSegment(sketch, "E188", {"start": v(142.88, 47.63) * mm, "end": v(146.05, 47.63) * mm});
            skLineSegment(sketch, "E189", {"start": v(146.05, 47.63) * mm, "end": v(146.05, 34.93) * mm});
            skLineSegment(sketch, "E190", {"start": v(146.05, 34.93) * mm, "end": v(142.88, 34.93) * mm});
            skLineSegment(sketch, "E191.trimOffspring", {"start": v(142.88, 34.93) * mm, "end": v(142.88, 28.58) * mm});
            skLineSegment(sketch, "E192.trimOffspring", {"start": v(130.18, 34.92) * mm, "end": v(130.18, 28.58) * mm});
            skLineSegment(sketch, "E193.trimOffspring", {"start": v(139.57, 28.58) * mm, "end": v(142.88, 28.58) * mm});
            skSolve(sketch);
        }
        {
            var Q0;
            Q0=makeQuery(id+"F48.imprint","IMPRINT",FACE,{"disambiguationData":[TD([[makeQuery(id+"F48.imprint","IMPRINT",EDGE,{"derivedFrom":sQuery(id+"F48.wireOp",EDGE,"E181.bottom")}),-1.0]])]});
            extrude(context, id + "F49", {"entities" : qUnion([Q0]), "depth" : 3.17 * mm});
        }
        {
            var Q0;
            Q0=makeQuery(id+"F49.opExtrude","SWEPT_BODY",BODY,{"disambiguationData":[OSD([sQuery(id+"F48.wireOp",EDGE,"E181.bottom"),sQuery(id+"F48.wireOp",EDGE,"E181.top"),sQuery(id+"F48.wireOp",EDGE,"E181.left"),sQuery(id+"F48.wireOp",EDGE,"E181.right"),sQuery(id+"F48.wireOp",EDGE,"E182"),sQuery(id+"F48.wireOp",EDGE,"E183"),sQuery(id+"F48.wireOp",EDGE,"E184"),sQuery(id+"F48.wireOp",EDGE,"E185"),sQuery(id+"F48.wireOp",EDGE,"E186"),sQuery(id+"F48.wireOp",EDGE,"E187"),sQuery(id+"F48.wireOp",EDGE,"E188"),sQuery(id+"F48.wireOp",EDGE,"E189"),sQuery(id+"F48.wireOp",EDGE,"E190"),sQuery(id+"F48.wireOp",EDGE,"E191.trimOffspring"),sQuery(id+"F48.wireOp",EDGE,"E192.trimOffspring"),sQuery(id+"F48.wireOp",EDGE,"E193.trimOffspring")])]});
            var Q1;
            Q1=qCreatedBy(makeId("Front.planeOp"),FACE);
            mirror(context, id + "F50", {"entities" : qUnion([Q0]), "mirrorPlane" : qUnion([Q1])});
        }
        {
            var Q0;
            Q0=makeQuery(id+"F47.opExtrude","CAP_FACE",FACE,{"disambiguationData":[OSD([sQuery(id+"F46.wireOp",EDGE,"E180")])],"isStart":false});
            var sketch = newSketch(context, id + "F51", { "sketchPlane" : qUnion([Q0])});
            skCircle(sketch, "E194", {"center": v(-136.53, 43.82) * mm, "radius": 22.23 * mm});
            skSolve(sketch);
        }
        {
            var Q0;
            Q0=makeQuery(id+"F51.imprint","IMPRINT",FACE,{"disambiguationData":[TD([[makeQuery(id+"F51.imprint","IMPRINT",EDGE,{"derivedFrom":sQuery(id+"F51.wireOp",EDGE,"E194")}),1.0]])]});
            var Q1;
            Q1=makeQuery(id+"F51.imprint","IMPRINT",FACE,{"disambiguationData":[TD([[makeQuery(id+"F51.imprint","IMPRINT",EDGE,{"derivedFrom":makeQuery(id+"F47.opExtrude","CAP_EDGE",EDGE,{"disambiguationData":[OSD([sQuery(id+"F46.wireOp",EDGE,"E180")])],"isStart":false})}),1.0]])]});
            extrude(context, id + "F52", {"entities" : qUnion([Q0, Q1]), "operationType" : NewBodyOperationType.ADD, "depth" : 6.35 * mm});
        }
        {
            var Q0;
            Q0=makeQuery(id+"F45.opExtrude","CAP_FACE",FACE,{"disambiguationData":[OSD([sQuery(id+"F44.wireOp",EDGE,"E179")])],"isStart":true});
            var sketch = newSketch(context, id + "F53", { "sketchPlane" : qUnion([Q0])});
            skCircle(sketch, "E195", {"center": v(0, 66.68) * mm, "radius": 22.23 * mm});
            skSolve(sketch);
        }
        {
            var Q0;
            Q0=makeQuery(id+"F53.imprint","IMPRINT",FACE,{"disambiguationData":[TD([[makeQuery(id+"F53.imprint","IMPRINT",EDGE,{"derivedFrom":makeQuery(id+"F45.opExtrude","CAP_EDGE",EDGE,{"disambiguationData":[OSD([sQuery(id+"F44.wireOp",EDGE,"E179")])],"isStart":true})}),-1.0]])]});
            var Q1;
            Q1=makeQuery(id+"F53.imprint","IMPRINT",FACE,{"disambiguationData":[TD([[makeQuery(id+"F53.imprint","IMPRINT",EDGE,{"derivedFrom":sQuery(id+"F53.wireOp",EDGE,"E195")}),1.0]])]});
            extrude(context, id + "F54", {"entities" : qUnion([Q0, Q1]), "operationType" : NewBodyOperationType.ADD, "depth" : 6.35 * mm});
        }
        {
            var Q0;
            Q0=qCreatedBy(id+"F28.planeOp",FACE);
            var sketch = newSketch(context, id + "F55", { "sketchPlane" : qUnion([Q0])});
            skLineSegment(sketch, "E196.bottom", {"start": v(-7.14, 69.85) * mm, "end": v(7.14, 69.85) * mm});
            skLineSegment(sketch, "E196.top", {"start": v(-7.14, 31.75) * mm, "end": v(7.14, 31.75) * mm});
            skLineSegment(sketch, "E196.left", {"start": v(-7.14, 69.85) * mm, "end": v(-7.14, 31.75) * mm});
            skLineSegment(sketch, "E196.right", {"start": v(7.14, 69.85) * mm, "end": v(7.14, 31.75) * mm});
            skLineSegment(sketch, "E197", {"start": v(-7.14, 53.34) * mm, "end": v(-10.32, 53.34) * mm});
            skLineSegment(sketch, "E198", {"start": v(-10.32, 53.34) * mm, "end": v(-10.32, 40.64) * mm});
            skLineSegment(sketch, "E199", {"start": v(-10.32, 40.64) * mm, "end": v(-7.14, 40.64) * mm});
            skLineSegment(sketch, "E200", {"start": v(7.14, 53.34) * mm, "end": v(10.32, 53.34) * mm});
            skLineSegment(sketch, "E201", {"start": v(10.32, 53.34) * mm, "end": v(10.32, 40.64) * mm});
            skLineSegment(sketch, "E202", {"start": v(10.32, 40.64) * mm, "end": v(7.14, 40.64) * mm});
            skSolve(sketch);
        }
        {
            var Q0;
            Q0 = qSketchRegion(id + "F55", true);
            extrude(context, id + "F56", {"entities" : qUnion([Q0]), "depth" : 3.17 * mm});
        }
        {
            var Q0;
            Q0=makeQuery(id+"F56.opExtrude","SWEPT_BODY",BODY,{"disambiguationData":[OSD([sQuery(id+"F55.wireOp",EDGE,"E196.bottom"),sQuery(id+"F55.wireOp",EDGE,"E196.top"),sQuery(id+"F55.wireOp",EDGE,"E196.left"),sQuery(id+"F55.wireOp",EDGE,"E196.right"),sQuery(id+"F55.wireOp",EDGE,"E197"),sQuery(id+"F55.wireOp",EDGE,"E198"),sQuery(id+"F55.wireOp",EDGE,"E199"),sQuery(id+"F55.wireOp",EDGE,"E200"),sQuery(id+"F55.wireOp",EDGE,"E201"),sQuery(id+"F55.wireOp",EDGE,"E202")])]});
            var Q1;
            Q1=qCreatedBy(makeId("Front.planeOp"),FACE);
            mirror(context, id + "F57", {"entities" : qUnion([Q0]), "mirrorPlane" : qUnion([Q1])});
        }
        {
            var Q0;
            Q0=qCreatedBy(makeId("Right.planeOp"),FACE);
            cPlane(context, id + "F58", {"entities" : qUnion([Q0]), "cplaneType" : CPlaneType.OFFSET, "offset" : 136.53 * mm, "oppositeDirection" : true, "width" : 152.4 * mm, "height" : 152.4 * mm});
        }
        {
            var Q0;
            Q0=qCreatedBy(makeId("Right.planeOp"),FACE);
            cPlane(context, id + "F59", {"entities" : qUnion([Q0]), "cplaneType" : CPlaneType.OFFSET, "offset" : 129.38 * mm, "oppositeDirection" : true, "width" : 152.4 * mm, "height" : 152.4 * mm});
        }
        {
            var Q0;
            Q0=qCreatedBy(id+"F59.planeOp",FACE);
            var sketch = newSketch(context, id + "F60", { "sketchPlane" : qUnion([Q0])});
            skLineSegment(sketch, "E203.bottom", {"start": v(4.17, 51.44) * mm, "end": v(-4.17, 51.44) * mm});
            skLineSegment(sketch, "E203.top", {"start": v(4.17, 38.74) * mm, "end": v(-4.17, 38.74) * mm});
            skLineSegment(sketch, "E203.left", {"start": v(4.17, 51.44) * mm, "end": v(4.17, 48.26) * mm});
            skLineSegment(sketch, "E203.right", {"start": v(-4.17, 51.44) * mm, "end": v(-4.17, 48.26) * mm});
            skLineSegment(sketch, "E204", {"start": v(-4.17, 48.26) * mm, "end": v(-7.34, 48.26) * mm});
            skLineSegment(sketch, "E205", {"start": v(-7.34, 48.26) * mm, "end": v(-7.34, 41.91) * mm});
            skLineSegment(sketch, "E206", {"start": v(-7.34, 41.91) * mm, "end": v(-4.17, 41.91) * mm});
            skLineSegment(sketch, "E207", {"start": v(4.17, 48.26) * mm, "end": v(7.34, 48.26) * mm});
            skLineSegment(sketch, "E208", {"start": v(7.34, 48.26) * mm, "end": v(7.34, 41.91) * mm});
            skLineSegment(sketch, "E209", {"start": v(7.34, 41.91) * mm, "end": v(4.17, 41.91) * mm});
            skLineSegment(sketch, "E210.trimOffspring", {"start": v(4.17, 41.91) * mm, "end": v(4.17, 38.74) * mm});
            skLineSegment(sketch, "E211.trimOffspring", {"start": v(-4.17, 41.91) * mm, "end": v(-4.17, 38.74) * mm});
            skSolve(sketch);
        }
        {
            var Q0;
            Q0 = qSketchRegion(id + "F60", true);
            extrude(context, id + "F61", {"entities" : qUnion([Q0]), "depth" : 3.17 * mm});
        }
        {
            var Q0;
            Q0=makeQuery(id+"F61.opExtrude","SWEPT_BODY",BODY,{"disambiguationData":[OSD([sQuery(id+"F60.wireOp",EDGE,"E203.bottom"),sQuery(id+"F60.wireOp",EDGE,"E203.top"),sQuery(id+"F60.wireOp",EDGE,"E203.left"),sQuery(id+"F60.wireOp",EDGE,"E203.right"),sQuery(id+"F60.wireOp",EDGE,"E204"),sQuery(id+"F60.wireOp",EDGE,"E205"),sQuery(id+"F60.wireOp",EDGE,"E206"),sQuery(id+"F60.wireOp",EDGE,"E207"),sQuery(id+"F60.wireOp",EDGE,"E208"),sQuery(id+"F60.wireOp",EDGE,"E209"),sQuery(id+"F60.wireOp",EDGE,"E210.trimOffspring"),sQuery(id+"F60.wireOp",EDGE,"E211.trimOffspring")])]});
            var Q1;
            Q1=qCreatedBy(id+"F58.planeOp",FACE);
            mirror(context, id + "F62", {"entities" : qUnion([Q0]), "mirrorPlane" : qUnion([Q1])});
        }
        {
            var Q0;
            Q0=makeQuery(id+"F6.boolean.opBoolean","MERGE",FACE,{"derivedFrom":[makeQuery(id+"F4.opExtrude","CAP_FACE",FACE,{"disambiguationData":[OSD([sQuery(id+"F3.wireOp",EDGE,"E1.bottom"),sQuery(id+"F3.wireOp",EDGE,"E1.top"),sQuery(id+"F3.wireOp",EDGE,"E1.left"),sQuery(id+"F3.wireOp",EDGE,"E1.right"),sQuery(id+"F3.wireOp",EDGE,"E2.bottom"),sQuery(id+"F3.wireOp",EDGE,"E2.top"),sQuery(id+"F3.wireOp",EDGE,"E7.right"),sQuery(id+"F3.wireOp",EDGE,"E8.right"),sQuery(id+"F3.wireOp",EDGE,"E13"),sQuery(id+"F3.wireOp",EDGE,"E14"),sQuery(id+"F3.wireOp",EDGE,"E15"),sQuery(id+"F3.wireOp",EDGE,"E16"),sQuery(id+"F3.wireOp",EDGE,"E17"),sQuery(id+"F3.wireOp",EDGE,"E18"),sQuery(id+"F3.wireOp",EDGE,"E19"),sQuery(id+"F3.wireOp",EDGE,"E20"),sQuery(id+"F3.wireOp",EDGE,"E21.filletArc"),sQuery(id+"F3.wireOp",EDGE,"E22.filletArc"),sQuery(id+"F3.wireOp",EDGE,"E23.filletArc"),sQuery(id+"F3.wireOp",EDGE,"E24.filletArc")])],"isStart":false}),makeQuery(id+"F6.opExtrude","CAP_FACE",FACE,{"disambiguationData":[OSD([sQuery(id+"F5.wireOp",EDGE,"E25.bottom"),sQuery(id+"F5.wireOp",EDGE,"E25.top"),sQuery(id+"F5.wireOp",EDGE,"E25.left"),sQuery(id+"F5.wireOp",EDGE,"E25.right"),sQuery(id+"F5.wireOp",EDGE,"E26.filletArc"),sQuery(id+"F5.wireOp",EDGE,"E27.filletArc"),sQuery(id+"F5.wireOp",EDGE,"E28.filletArc"),sQuery(id+"F5.wireOp",EDGE,"E29.filletArc")])],"isStart":true})]});
            var sketch = newSketch(context, id + "F63", { "sketchPlane" : qUnion([Q0])});
            skLineSegment(sketch, "E212.0", {"start": v(-85.73, 120.65) * mm, "end": v(-85.73, 107.95) * mm});
            skLineSegment(sketch, "E213.0", {"start": v(-85.73, 120.65) * mm, "end": v(-88.9, 120.65) * mm});
            skLineSegment(sketch, "E214.0", {"start": v(-88.9, 120.65) * mm, "end": v(-88.9, 107.95) * mm});
            skLineSegment(sketch, "E215.0", {"start": v(-85.73, 107.95) * mm, "end": v(-88.9, 107.95) * mm});
            skLineSegment(sketch, "E216.0", {"start": v(-107.95, 88.9) * mm, "end": v(-120.65, 88.9) * mm});
            skPoint(sketch, "E217.0", {"position": v(-120.65, 87.31) * mm});
            skLineSegment(sketch, "E218.0", {"start": v(-120.65, 85.73) * mm, "end": v(-120.65, 88.9) * mm});
            skLineSegment(sketch, "E219.0", {"start": v(-107.95, 85.73) * mm, "end": v(-120.65, 85.73) * mm});
            skLineSegment(sketch, "E220.0", {"start": v(-107.95, 85.73) * mm, "end": v(-107.95, 88.9) * mm});
            skLineSegment(sketch, "E221.0", {"start": v(88.9, 120.65) * mm, "end": v(88.9, 107.95) * mm});
            skLineSegment(sketch, "E222.0", {"start": v(85.73, 120.65) * mm, "end": v(88.9, 120.65) * mm});
            skLineSegment(sketch, "E223.0", {"start": v(85.73, 120.65) * mm, "end": v(85.73, 107.95) * mm});
            skLineSegment(sketch, "E224.0", {"start": v(85.73, 107.95) * mm, "end": v(88.9, 107.95) * mm});
            skLineSegment(sketch, "E225.0", {"start": v(107.95, 88.9) * mm, "end": v(120.65, 88.9) * mm});
            skLineSegment(sketch, "E226.0", {"start": v(120.65, 85.73) * mm, "end": v(120.65, 88.9) * mm});
            skLineSegment(sketch, "E227.0", {"start": v(107.95, 85.73) * mm, "end": v(120.65, 85.73) * mm});
            skLineSegment(sketch, "E228.0", {"start": v(107.95, 85.73) * mm, "end": v(107.95, 88.9) * mm});
            skLineSegment(sketch, "E229.0", {"start": v(107.95, -88.9) * mm, "end": v(120.65, -88.9) * mm});
            skLineSegment(sketch, "E230.0", {"start": v(107.95, -85.73) * mm, "end": v(107.95, -88.9) * mm});
            skLineSegment(sketch, "E231.0", {"start": v(107.95, -85.73) * mm, "end": v(120.65, -85.73) * mm});
            skLineSegment(sketch, "E232.0", {"start": v(120.65, -85.73) * mm, "end": v(120.65, -88.9) * mm});
            skLineSegment(sketch, "E233.0", {"start": v(88.9, -120.65) * mm, "end": v(88.9, -107.95) * mm});
            skLineSegment(sketch, "E234.0", {"start": v(85.73, -107.95) * mm, "end": v(88.9, -107.95) * mm});
            skLineSegment(sketch, "E235.0", {"start": v(85.73, -120.65) * mm, "end": v(85.73, -107.95) * mm});
            skLineSegment(sketch, "E236.0", {"start": v(85.73, -120.65) * mm, "end": v(88.9, -120.65) * mm});
            skLineSegment(sketch, "E237.0", {"start": v(-85.73, -120.65) * mm, "end": v(-85.73, -107.95) * mm});
            skLineSegment(sketch, "E238.0", {"start": v(-85.73, -107.95) * mm, "end": v(-88.9, -107.95) * mm});
            skLineSegment(sketch, "E239.0", {"start": v(-88.9, -120.65) * mm, "end": v(-88.9, -107.95) * mm});
            skLineSegment(sketch, "E240.0", {"start": v(-85.73, -120.65) * mm, "end": v(-88.9, -120.65) * mm});
            skLineSegment(sketch, "E241.0", {"start": v(-107.95, -85.73) * mm, "end": v(-120.65, -85.73) * mm});
            skLineSegment(sketch, "E242.0", {"start": v(-120.65, -85.73) * mm, "end": v(-120.65, -88.9) * mm});
            skLineSegment(sketch, "E243.0", {"start": v(-107.95, -88.9) * mm, "end": v(-120.65, -88.9) * mm});
            skLineSegment(sketch, "E244.0", {"start": v(-107.95, -85.73) * mm, "end": v(-107.95, -88.9) * mm});
            skSolve(sketch);
        }
        {
            var Q0;
            Q0 = qSketchRegion(id + "F63", true);
            extrude(context, id + "F64", {"entities" : qUnion([Q0]), "operationType" : NewBodyOperationType.REMOVE, "oppositeDirection" : true, "depth" : 25.4 * mm});
        }
        {
            var Q0;
            Q0=makeQuery(id+"F6.boolean.opBoolean","MERGE",FACE,{"derivedFrom":[makeQuery(id+"F4.opExtrude","CAP_FACE",FACE,{"disambiguationData":[OSD([sQuery(id+"F3.wireOp",EDGE,"E1.bottom"),sQuery(id+"F3.wireOp",EDGE,"E1.top"),sQuery(id+"F3.wireOp",EDGE,"E1.left"),sQuery(id+"F3.wireOp",EDGE,"E1.right"),sQuery(id+"F3.wireOp",EDGE,"E2.bottom"),sQuery(id+"F3.wireOp",EDGE,"E2.top"),sQuery(id+"F3.wireOp",EDGE,"E7.right"),sQuery(id+"F3.wireOp",EDGE,"E8.right"),sQuery(id+"F3.wireOp",EDGE,"E13"),sQuery(id+"F3.wireOp",EDGE,"E14"),sQuery(id+"F3.wireOp",EDGE,"E15"),sQuery(id+"F3.wireOp",EDGE,"E16"),sQuery(id+"F3.wireOp",EDGE,"E17"),sQuery(id+"F3.wireOp",EDGE,"E18"),sQuery(id+"F3.wireOp",EDGE,"E19"),sQuery(id+"F3.wireOp",EDGE,"E20"),sQuery(id+"F3.wireOp",EDGE,"E21.filletArc"),sQuery(id+"F3.wireOp",EDGE,"E22.filletArc"),sQuery(id+"F3.wireOp",EDGE,"E23.filletArc"),sQuery(id+"F3.wireOp",EDGE,"E24.filletArc")])],"isStart":true}),makeQuery(id+"F6.opExtrude","CAP_FACE",FACE,{"disambiguationData":[OSD([sQuery(id+"F5.wireOp",EDGE,"E25.bottom"),sQuery(id+"F5.wireOp",EDGE,"E25.top"),sQuery(id+"F5.wireOp",EDGE,"E25.left"),sQuery(id+"F5.wireOp",EDGE,"E25.right"),sQuery(id+"F5.wireOp",EDGE,"E26.filletArc"),sQuery(id+"F5.wireOp",EDGE,"E27.filletArc"),sQuery(id+"F5.wireOp",EDGE,"E28.filletArc"),sQuery(id+"F5.wireOp",EDGE,"E29.filletArc")])],"isStart":false})]});
            var sketch = newSketch(context, id + "F65", { "sketchPlane" : qUnion([Q0])});
            skLineSegment(sketch, "E245.0", {"start": v(-161.93, 127) * mm, "end": v(-149.23, 127) * mm});
            skLineSegment(sketch, "E246.0", {"start": v(-161.93, 123.83) * mm, "end": v(-161.93, 127) * mm});
            skLineSegment(sketch, "E247.0", {"start": v(-161.93, 123.83) * mm, "end": v(-149.23, 123.83) * mm});
            skLineSegment(sketch, "E248.0", {"start": v(-149.23, 123.83) * mm, "end": v(-149.23, 127) * mm});
            skLineSegment(sketch, "E249.0", {"start": v(-149.23, 117.48) * mm, "end": v(-149.23, 114.3) * mm});
            skLineSegment(sketch, "E250.0", {"start": v(-161.93, 117.48) * mm, "end": v(-149.23, 117.48) * mm});
            skLineSegment(sketch, "E251.0", {"start": v(-161.93, 114.3) * mm, "end": v(-149.23, 114.3) * mm});
            skLineSegment(sketch, "E252.0", {"start": v(-161.93, 117.48) * mm, "end": v(-161.93, 114.3) * mm});
            skLineSegment(sketch, "E253.0", {"start": v(-111.13, 123.83) * mm, "end": v(-111.13, 127) * mm});
            skLineSegment(sketch, "E254.0", {"start": v(-123.83, 123.83) * mm, "end": v(-111.13, 123.83) * mm});
            skLineSegment(sketch, "E255.0", {"start": v(-123.83, 127) * mm, "end": v(-111.13, 127) * mm});
            skLineSegment(sketch, "E256.0", {"start": v(-123.83, 123.83) * mm, "end": v(-123.83, 127) * mm});
            skLineSegment(sketch, "E257.0", {"start": v(-123.83, 117.48) * mm, "end": v(-123.83, 114.3) * mm});
            skLineSegment(sketch, "E258.0", {"start": v(-123.83, 117.48) * mm, "end": v(-111.13, 117.48) * mm});
            skLineSegment(sketch, "E259.0", {"start": v(-123.83, 114.3) * mm, "end": v(-111.13, 114.3) * mm});
            skLineSegment(sketch, "E260.0", {"start": v(-111.13, 117.48) * mm, "end": v(-111.13, 114.3) * mm});
            skLineSegment(sketch, "E261.0", {"start": v(-123.83, -117.48) * mm, "end": v(-111.13, -117.48) * mm});
            skLineSegment(sketch, "E262.0", {"start": v(-123.83, -117.48) * mm, "end": v(-123.83, -114.3) * mm});
            skLineSegment(sketch, "E263.0", {"start": v(-123.83, -114.3) * mm, "end": v(-111.13, -114.3) * mm});
            skLineSegment(sketch, "E264.0", {"start": v(-111.13, -117.48) * mm, "end": v(-111.13, -114.3) * mm});
            skLineSegment(sketch, "E265.0", {"start": v(-111.13, -123.83) * mm, "end": v(-111.13, -127) * mm});
            skLineSegment(sketch, "E266.0", {"start": v(-123.83, -123.83) * mm, "end": v(-111.13, -123.83) * mm});
            skLineSegment(sketch, "E267.0", {"start": v(-123.83, -127) * mm, "end": v(-111.13, -127) * mm});
            skLineSegment(sketch, "E268.0", {"start": v(-123.83, -123.83) * mm, "end": v(-123.83, -127) * mm});
            skLineSegment(sketch, "E269.0", {"start": v(-149.23, -123.83) * mm, "end": v(-149.23, -127) * mm});
            skLineSegment(sketch, "E270.0", {"start": v(-161.93, -123.83) * mm, "end": v(-149.23, -123.83) * mm});
            skLineSegment(sketch, "E271.0", {"start": v(-161.93, -127) * mm, "end": v(-149.23, -127) * mm});
            skLineSegment(sketch, "E272.0", {"start": v(-161.93, -123.83) * mm, "end": v(-161.93, -127) * mm});
            skLineSegment(sketch, "E273.0", {"start": v(-161.93, -117.48) * mm, "end": v(-149.23, -117.48) * mm});
            skLineSegment(sketch, "E274.0", {"start": v(-161.93, -117.48) * mm, "end": v(-161.93, -114.3) * mm});
            skLineSegment(sketch, "E275.0", {"start": v(-161.93, -114.3) * mm, "end": v(-149.23, -114.3) * mm});
            skLineSegment(sketch, "E276.0", {"start": v(-149.23, -117.48) * mm, "end": v(-149.23, -114.3) * mm});
            skSolve(sketch);
        }
        {
            var Q0;
            Q0 = qSketchRegion(id + "F65", true);
            extrude(context, id + "F66", {"entities" : qUnion([Q0]), "operationType" : NewBodyOperationType.REMOVE, "oppositeDirection" : true, "depth" : 25.4 * mm});
        }
        {
            var Q0;
            Q0=makeQuery(id+"F31.opExtrude","CAP_FACE",FACE,{"disambiguationData":[OSD([sQuery(id+"F30.wireOp",EDGE,"E140.bottom"),sQuery(id+"F30.wireOp",EDGE,"E140.left"),sQuery(id+"F30.wireOp",EDGE,"E140.right"),sQuery(id+"F30.wireOp",EDGE,"E141"),sQuery(id+"F30.wireOp",EDGE,"E142"),sQuery(id+"F30.wireOp",EDGE,"E143"),sQuery(id+"F30.wireOp",EDGE,"E144"),sQuery(id+"F30.wireOp",EDGE,"E145"),sQuery(id+"F30.wireOp",EDGE,"E146"),sQuery(id+"F30.wireOp",EDGE,"E147"),sQuery(id+"F30.wireOp",EDGE,"E150"),sQuery(id+"F30.wireOp",EDGE,"E151"),sQuery(id+"F30.wireOp",EDGE,"E152"),sQuery(id+"F30.wireOp",EDGE,"E153.trimOffspring"),sQuery(id+"F30.wireOp",EDGE,"E154"),sQuery(id+"F30.wireOp",EDGE,"E155"),sQuery(id+"F30.wireOp",EDGE,"E156")])],"isStart":false});
            var sketch = newSketch(context, id + "F67", { "sketchPlane" : qUnion([Q0])});
            skLineSegment(sketch, "E277.0", {"start": v(-143.67, 48.26) * mm, "end": v(-143.67, 41.91) * mm});
            skLineSegment(sketch, "E278.0", {"start": v(-146.84, 48.26) * mm, "end": v(-143.67, 48.26) * mm});
            skLineSegment(sketch, "E279.0", {"start": v(-146.84, 48.26) * mm, "end": v(-146.84, 41.91) * mm});
            skLineSegment(sketch, "E280.0", {"start": v(-146.84, 41.91) * mm, "end": v(-143.67, 41.91) * mm});
            skLineSegment(sketch, "E281.0", {"start": v(-126.2, 41.91) * mm, "end": v(-129.38, 41.91) * mm});
            skLineSegment(sketch, "E282.0", {"start": v(-129.38, 48.26) * mm, "end": v(-129.38, 41.91) * mm});
            skLineSegment(sketch, "E283.0", {"start": v(-126.2, 48.26) * mm, "end": v(-129.38, 48.26) * mm});
            skLineSegment(sketch, "E284.0", {"start": v(-126.2, 48.26) * mm, "end": v(-126.2, 41.91) * mm});
            skSolve(sketch);
        }
        {
            var Q0;
            Q0 = qSketchRegion(id + "F67", true);
            extrude(context, id + "F68", {"entities" : qUnion([Q0]), "operationType" : NewBodyOperationType.REMOVE, "oppositeDirection" : true, "depth" : 25.4 * mm});
        }
        {
            var Q0;
            Q0=makeQuery(id+"F27.opPattern","COPY",FACE,{"derivedFrom":makeQuery(id+"F26.opExtrude","CAP_FACE",FACE,{"disambiguationData":[OSD([sQuery(id+"F25.wireOp",EDGE,"E129"),sQuery(id+"F25.wireOp",EDGE,"E130"),sQuery(id+"F25.wireOp",EDGE,"E131"),sQuery(id+"F25.wireOp",EDGE,"E132"),sQuery(id+"F25.wireOp",EDGE,"E133"),sQuery(id+"F25.wireOp",EDGE,"E134"),sQuery(id+"F25.wireOp",EDGE,"E135"),sQuery(id+"F25.wireOp",EDGE,"E138.filletArc"),sQuery(id+"F25.wireOp",EDGE,"E139.filletArc")])],"isStart":true}),"instanceName":"1"});
            var sketch = newSketch(context, id + "F69", { "sketchPlane" : qUnion([Q0])});
            skLineSegment(sketch, "E285.0", {"start": v(7.34, 47.63) * mm, "end": v(7.34, 34.93) * mm});
            skLineSegment(sketch, "E286.0", {"start": v(4.17, 47.63) * mm, "end": v(4.17, 34.93) * mm});
            skLineSegment(sketch, "E287.0", {"start": v(7.34, 34.93) * mm, "end": v(4.17, 34.93) * mm});
            skLineSegment(sketch, "E288.0", {"start": v(7.34, 47.63) * mm, "end": v(4.17, 47.63) * mm});
            skLineSegment(sketch, "E289.0", {"start": v(-7.34, 34.93) * mm, "end": v(-4.17, 34.93) * mm});
            skLineSegment(sketch, "E290.0", {"start": v(-4.17, 47.63) * mm, "end": v(-4.17, 34.93) * mm});
            skLineSegment(sketch, "E291.0", {"start": v(-7.34, 47.63) * mm, "end": v(-7.34, 34.93) * mm});
            skLineSegment(sketch, "E292.0", {"start": v(-7.34, 47.63) * mm, "end": v(-4.17, 47.63) * mm});
            skSolve(sketch);
        }
        {
            var Q0;
            Q0 = qSketchRegion(id + "F69", true);
            extrude(context, id + "F70", {"entities" : qUnion([Q0]), "operationType" : NewBodyOperationType.REMOVE, "oppositeDirection" : true, "depth" : 51.05 * mm});
        }
        {
            var Q0;
            Q0=makeQuery(id+"F43.opPattern","COPY",FACE,{"derivedFrom":makeQuery(id+"F42.opExtrude","CAP_FACE",FACE,{"disambiguationData":[OSD([sQuery(id+"F41.wireOp",EDGE,"E170"),sQuery(id+"F41.wireOp",EDGE,"E171"),sQuery(id+"F41.wireOp",EDGE,"E172"),sQuery(id+"F41.wireOp",EDGE,"E173"),sQuery(id+"F41.wireOp",EDGE,"E174"),sQuery(id+"F41.wireOp",EDGE,"E175.filletArc"),sQuery(id+"F41.wireOp",EDGE,"E176.filletArc"),sQuery(id+"F41.wireOp",EDGE,"E177"),sQuery(id+"F41.wireOp",EDGE,"E178")])],"isStart":false}),"instanceName":"1"});
            var sketch = newSketch(context, id + "F71", { "sketchPlane" : qUnion([Q0])});
            skLineSegment(sketch, "E293.0", {"start": v(10.32, 53.34) * mm, "end": v(10.32, 40.64) * mm});
            skLineSegment(sketch, "E294.0", {"start": v(10.32, 53.34) * mm, "end": v(7.14, 53.34) * mm});
            skLineSegment(sketch, "E295.0", {"start": v(7.14, 53.34) * mm, "end": v(7.14, 40.64) * mm});
            skLineSegment(sketch, "E296.0", {"start": v(10.32, 40.64) * mm, "end": v(7.14, 40.64) * mm});
            skLineSegment(sketch, "E297.0", {"start": v(-10.32, 40.64) * mm, "end": v(-7.14, 40.64) * mm});
            skLineSegment(sketch, "E298.0", {"start": v(-7.14, 53.34) * mm, "end": v(-7.14, 40.64) * mm});
            skLineSegment(sketch, "E299.0", {"start": v(-10.32, 53.34) * mm, "end": v(-10.32, 40.64) * mm});
            skLineSegment(sketch, "E300.0", {"start": v(-10.32, 53.34) * mm, "end": v(-7.14, 53.34) * mm});
            skSolve(sketch);
        }
        {
            var Q0;
            Q0 = qSketchRegion(id + "F71", true);
            extrude(context, id + "F72", {"entities" : qUnion([Q0]), "operationType" : NewBodyOperationType.REMOVE, "oppositeDirection" : true, "depth" : 25.4 * mm});
        }
        {
            var Q0;
            Q0=makeQuery(id+"F37.opPattern","COPY",FACE,{"derivedFrom":makeQuery(id+"F35.opExtrude","CAP_FACE",FACE,{"disambiguationData":[OSD([sQuery(id+"F34.wireOp",EDGE,"E160.0"),sQuery(id+"F34.wireOp",EDGE,"E161.0"),sQuery(id+"F34.wireOp",EDGE,"E162.0"),sQuery(id+"F34.wireOp",EDGE,"E157.0"),sQuery(id+"F34.wireOp",EDGE,"E163.0"),sQuery(id+"F34.wireOp",EDGE,"E164.0"),sQuery(id+"F34.wireOp",EDGE,"E165.0"),sQuery(id+"F34.wireOp",EDGE,"E166.0"),sQuery(id+"F34.wireOp",EDGE,"E167.0")])],"isStart":true}),"instanceName":"1"});
            var sketch = newSketch(context, id + "F73", { "sketchPlane" : qUnion([Q0])});
            skLineSegment(sketch, "E301.0", {"start": v(-10.32, 47.63) * mm, "end": v(-10.32, 34.93) * mm});
            skLineSegment(sketch, "E302.0", {"start": v(-7.14, 47.63) * mm, "end": v(-7.14, 34.93) * mm});
            skLineSegment(sketch, "E303.0", {"start": v(-10.32, 47.63) * mm, "end": v(-7.14, 47.63) * mm});
            skLineSegment(sketch, "E304.0", {"start": v(-10.32, 34.93) * mm, "end": v(-7.14, 34.93) * mm});
            skLineSegment(sketch, "E305.0", {"start": v(10.32, 34.93) * mm, "end": v(7.14, 34.93) * mm});
            skLineSegment(sketch, "E306.0", {"start": v(7.14, 47.63) * mm, "end": v(7.14, 34.93) * mm});
            skLineSegment(sketch, "E307.0", {"start": v(10.32, 47.63) * mm, "end": v(10.32, 34.93) * mm});
            skLineSegment(sketch, "E308.0", {"start": v(10.32, 47.63) * mm, "end": v(7.14, 47.63) * mm});
            skSolve(sketch);
        }
        {
            var Q0;
            Q0 = qSketchRegion(id + "F73", true);
            extrude(context, id + "F74", {"entities" : qUnion([Q0]), "operationType" : NewBodyOperationType.REMOVE, "oppositeDirection" : true, "depth" : 25.4 * mm});
        }
        {
            var Q0;
            Q0=makeQuery(id+"F1.opExtrude","CAP_FACE",FACE,{"disambiguationData":[OSD([sQuery(id+"F0.wireOp",EDGE,"E0.bottom"),sQuery(id+"F0.wireOp",EDGE,"E0.top"),sQuery(id+"F0.wireOp",EDGE,"E0.left"),sQuery(id+"F0.wireOp",EDGE,"E0.right")])],"isStart":true});
            var sketch = newSketch(context, id + "F75", { "sketchPlane" : qUnion([Q0])});
            skLineSegment(sketch, "E309.0", {"start": v(-85.73, 93.66) * mm, "end": v(-85.73, 88.9) * mm});
            skLineSegment(sketch, "E310.0", {"start": v(-85.73, 93.66) * mm, "end": v(-88.9, 93.66) * mm});
            skLineSegment(sketch, "E311.0", {"start": v(-88.9, 93.66) * mm, "end": v(-88.9, 88.9) * mm});
            skLineSegment(sketch, "E312.0", {"start": v(-93.66, 88.9) * mm, "end": v(-88.9, 88.9) * mm});
            skLineSegment(sketch, "E313.0", {"start": v(-93.66, 85.73) * mm, "end": v(-93.66, 88.9) * mm});
            skLineSegment(sketch, "E314.0", {"start": v(-93.66, 85.73) * mm, "end": v(-88.9, 85.73) * mm});
            skLineSegment(sketch, "E315.0", {"start": v(-85.73, 80.96) * mm, "end": v(-88.9, 80.96) * mm});
            skLineSegment(sketch, "E316.0", {"start": v(93.66, 85.73) * mm, "end": v(93.66, 88.9) * mm});
            skLineSegment(sketch, "E317.0", {"start": v(93.66, 88.9) * mm, "end": v(88.9, 88.9) * mm});
            skLineSegment(sketch, "E318.0", {"start": v(88.9, 93.66) * mm, "end": v(88.9, 88.9) * mm});
            skLineSegment(sketch, "E319.0", {"start": v(85.73, 93.66) * mm, "end": v(85.73, 88.9) * mm});
            skLineSegment(sketch, "E320.0", {"start": v(93.66, 85.73) * mm, "end": v(88.9, 85.73) * mm});
            skLineSegment(sketch, "E321.0", {"start": v(85.73, 80.96) * mm, "end": v(88.9, 80.96) * mm});
            skLineSegment(sketch, "E322.0", {"start": v(85.73, 93.66) * mm, "end": v(88.9, 93.66) * mm});
            skLineSegment(sketch, "E323.trimOffspring", {"start": v(85.73, 85.73) * mm, "end": v(85.73, 80.96) * mm});
            skLineSegment(sketch, "E324.trimOffspring", {"start": v(88.9, 85.73) * mm, "end": v(88.9, 80.96) * mm});
            skLineSegment(sketch, "E325.trimOffspring", {"start": v(-88.9, 85.73) * mm, "end": v(-88.9, 80.96) * mm});
            skLineSegment(sketch, "E326.trimOffspring", {"start": v(-85.73, 85.73) * mm, "end": v(-85.73, 80.96) * mm});
            skLineSegment(sketch, "E327.0", {"start": v(-88.9, -93.66) * mm, "end": v(-88.9, -88.9) * mm});
            skLineSegment(sketch, "E328.0", {"start": v(-93.66, -85.73) * mm, "end": v(-88.9, -85.73) * mm});
            skLineSegment(sketch, "E329.0", {"start": v(-93.66, -85.73) * mm, "end": v(-93.66, -88.9) * mm});
            skLineSegment(sketch, "E330.0", {"start": v(-93.66, -88.9) * mm, "end": v(-88.9, -88.9) * mm});
            skLineSegment(sketch, "E331.0", {"start": v(-85.73, -93.66) * mm, "end": v(-85.73, -88.9) * mm});
            skLineSegment(sketch, "E332.0", {"start": v(-85.73, -93.66) * mm, "end": v(-88.9, -93.66) * mm});
            skLineSegment(sketch, "E333.0", {"start": v(-85.73, -80.96) * mm, "end": v(-88.9, -80.96) * mm});
            skLineSegment(sketch, "E334.trimOffspring", {"start": v(-85.73, -85.73) * mm, "end": v(-85.73, -80.96) * mm});
            skLineSegment(sketch, "E335.trimOffspring", {"start": v(-88.9, -85.73) * mm, "end": v(-88.9, -80.96) * mm});
            skLineSegment(sketch, "E336.0", {"start": v(88.9, -93.66) * mm, "end": v(88.9, -88.9) * mm});
            skLineSegment(sketch, "E337.0", {"start": v(85.73, -93.66) * mm, "end": v(85.73, -88.9) * mm});
            skLineSegment(sketch, "E338.0", {"start": v(93.66, -85.73) * mm, "end": v(88.9, -85.73) * mm});
            skLineSegment(sketch, "E339.0", {"start": v(93.66, -88.9) * mm, "end": v(88.9, -88.9) * mm});
            skLineSegment(sketch, "E340.0", {"start": v(93.66, -85.73) * mm, "end": v(93.66, -88.9) * mm});
            skLineSegment(sketch, "E341.0", {"start": v(85.73, -80.96) * mm, "end": v(88.9, -80.96) * mm});
            skLineSegment(sketch, "E342.0", {"start": v(85.73, -93.66) * mm, "end": v(88.9, -93.66) * mm});
            skLineSegment(sketch, "E343.trimOffspring", {"start": v(88.9, -85.73) * mm, "end": v(88.9, -80.96) * mm});
            skLineSegment(sketch, "E344.trimOffspring", {"start": v(85.73, -85.73) * mm, "end": v(85.73, -80.96) * mm});
            skLineSegment(sketch, "E345.0", {"start": v(-85.73, 88.9) * mm, "end": v(-80.96, 88.9) * mm});
            skLineSegment(sketch, "E346.0", {"start": v(-80.96, 85.73) * mm, "end": v(-80.96, 88.9) * mm});
            skLineSegment(sketch, "E347.0", {"start": v(-85.73, 85.73) * mm, "end": v(-80.96, 85.73) * mm});
            skPoint(sketch, "E348.0.end.orphan", {"position": v(-88.9, 88.9) * mm});
            skPoint(sketch, "E349.trimOffspring.end.orphan", {"position": v(-88.9, 85.73) * mm});
            skLineSegment(sketch, "E350.0", {"start": v(85.73, 88.9) * mm, "end": v(80.96, 88.9) * mm});
            skLineSegment(sketch, "E351.0", {"start": v(80.96, 85.73) * mm, "end": v(80.96, 88.9) * mm});
            skLineSegment(sketch, "E352.0", {"start": v(85.73, 85.73) * mm, "end": v(80.96, 85.73) * mm});
            skLineSegment(sketch, "E353.0", {"start": v(85.73, -85.73) * mm, "end": v(80.96, -85.73) * mm});
            skLineSegment(sketch, "E354.0", {"start": v(80.96, -85.73) * mm, "end": v(80.96, -88.9) * mm});
            skLineSegment(sketch, "E355.0", {"start": v(85.73, -88.9) * mm, "end": v(80.96, -88.9) * mm});
            skLineSegment(sketch, "E356.0", {"start": v(-85.73, -85.73) * mm, "end": v(-80.96, -85.73) * mm});
            skLineSegment(sketch, "E357.0", {"start": v(-85.73, -88.9) * mm, "end": v(-80.96, -88.9) * mm});
            skLineSegment(sketch, "E358.0", {"start": v(-80.96, -85.73) * mm, "end": v(-80.96, -88.9) * mm});
            skPoint(sketch, "E359.trimOffspring.end.orphan", {"position": v(-88.9, -85.73) * mm});
            skPoint(sketch, "E360.trimOffspring.end.orphan", {"position": v(-88.9, -88.9) * mm});
            skSolve(sketch);
        }
        {
            var Q0;
            Q0 = qSketchRegion(id + "F75", true);
            extrude(context, id + "F76", {"entities" : qUnion([Q0]), "operationType" : NewBodyOperationType.REMOVE, "oppositeDirection" : true, "depth" : 25.4 * mm});
        }
    });
